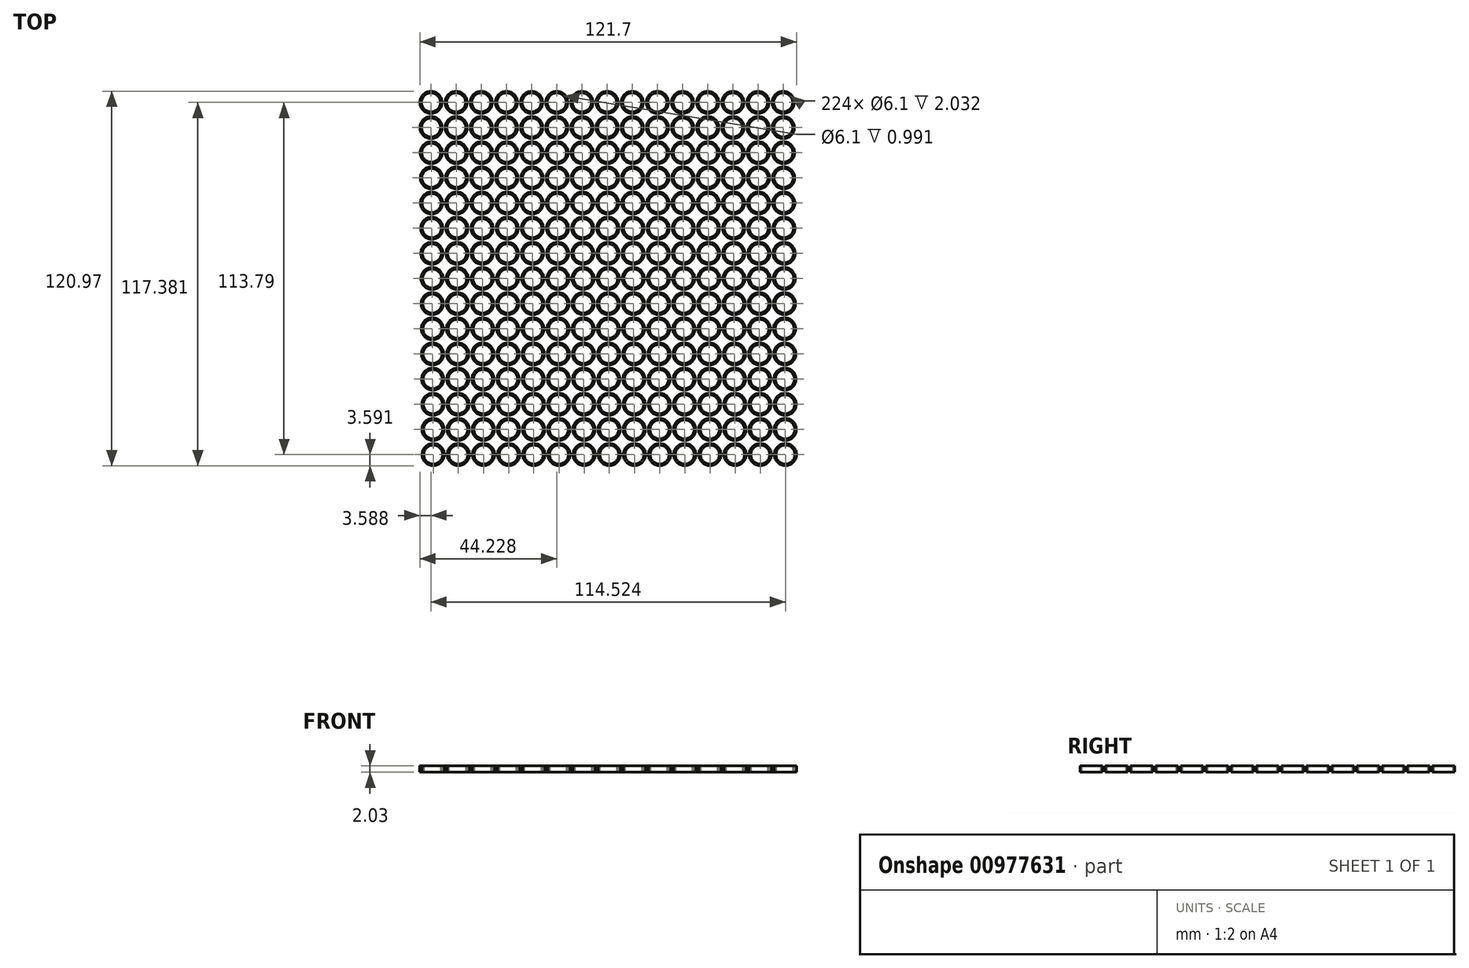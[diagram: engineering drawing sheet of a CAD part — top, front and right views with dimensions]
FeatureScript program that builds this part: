
annotation { "Feature Type Name" : "Feature", "Feature Type Description" : "" }
export const myFeature = defineFeature(function(context is Context, id is Id, definition is map)
    precondition{}
    {
        {
            var Q0;
            Q0=qCreatedBy(makeId("Top.planeOp"),FACE);
            var sketch = newSketch(context, id + "F0", { "sketchPlane" : qUnion([Q0])});
            skCircle(sketch, "E0", {"center": v(-60.84, 14.37) * mm, "radius": 3.6 * mm});
            skCircle(sketch, "E1.1.0.0", {"center": v(-52.71, 14.37) * mm, "radius": 3.6 * mm});
            skCircle(sketch, "E1.2.0.0", {"center": v(-44.59, 14.37) * mm, "radius": 3.6 * mm});
            skCircle(sketch, "E1.3.0.0", {"center": v(-36.46, 14.37) * mm, "radius": 3.6 * mm});
            skLineSegment(sketch, "E1.direction1", {"start": v(-60.84, 14.37) * mm, "end": v(-52.71, 14.37) * mm, "construction": true});
            skCircle(sketch, "E2.0.4.0", {"center": v(-28.33, 14.37) * mm, "radius": 3.6 * mm});
            skLineSegment(sketch, "E3.left", {"start": v(-60.84, 14.37) * mm, "end": v(-60.84, 14.37) * mm});
            skLineSegment(sketch, "E3.right", {"start": v(-28.33, 14.37) * mm, "end": v(-28.33, 14.37) * mm});
            skCircle(sketch, "E4", {"center": v(-60.84, 14.37) * mm, "radius": 3.05 * mm});
            skCircle(sketch, "E5.1.0.0", {"center": v(-52.71, 14.37) * mm, "radius": 3.05 * mm});
            skCircle(sketch, "E5.2.0.0", {"center": v(-44.59, 14.37) * mm, "radius": 3.05 * mm});
            skCircle(sketch, "E5.3.0.0", {"center": v(-36.46, 14.37) * mm, "radius": 3.05 * mm});
            skCircle(sketch, "E5.4.0.0", {"center": v(-28.33, 14.37) * mm, "radius": 3.05 * mm});
            skCircle(sketch, "E6", {"center": v(-60.84, 14.37) * mm, "radius": 2.54 * mm});
            skCircle(sketch, "E7.1.0.0", {"center": v(-52.71, 14.37) * mm, "radius": 2.54 * mm});
            skCircle(sketch, "E7.2.0.0", {"center": v(-44.59, 14.37) * mm, "radius": 2.54 * mm});
            skCircle(sketch, "E7.3.0.0", {"center": v(-36.46, 14.37) * mm, "radius": 2.54 * mm});
            skCircle(sketch, "E7.4.0.0", {"center": v(-28.33, 14.37) * mm, "radius": 2.54 * mm});
            skCircle(sketch, "E8.0.5.0", {"center": v(-20.2, 14.37) * mm, "radius": 2.54 * mm});
            skCircle(sketch, "E8.0.6.0", {"center": v(-12.07, 14.37) * mm, "radius": 2.54 * mm});
            skCircle(sketch, "E8.0.7.0", {"center": v(-3.95, 14.37) * mm, "radius": 2.54 * mm});
            skCircle(sketch, "E8.0.8.0", {"center": v(4.18, 14.37) * mm, "radius": 2.54 * mm});
            skCircle(sketch, "E8.0.9.0", {"center": v(12.31, 14.37) * mm, "radius": 2.54 * mm});
            skCircle(sketch, "E8.0.10.0", {"center": v(20.44, 14.37) * mm, "radius": 2.54 * mm});
            skCircle(sketch, "E8.0.11.0", {"center": v(28.57, 14.37) * mm, "radius": 2.54 * mm});
            skCircle(sketch, "E8.0.12.0", {"center": v(36.7, 14.37) * mm, "radius": 2.54 * mm});
            skCircle(sketch, "E8.0.13.0", {"center": v(44.82, 14.37) * mm, "radius": 2.54 * mm});
            skCircle(sketch, "E8.0.14.0", {"center": v(52.95, 14.37) * mm, "radius": 2.54 * mm});
            skCircle(sketch, "E9.0.5.0", {"center": v(-20.2, 14.37) * mm, "radius": 3.6 * mm});
            skCircle(sketch, "E9.0.6.0", {"center": v(-12.07, 14.37) * mm, "radius": 3.6 * mm});
            skCircle(sketch, "E9.0.7.0", {"center": v(-3.95, 14.37) * mm, "radius": 3.6 * mm});
            skCircle(sketch, "E9.0.8.0", {"center": v(4.18, 14.37) * mm, "radius": 3.6 * mm});
            skCircle(sketch, "E9.0.9.0", {"center": v(12.31, 14.37) * mm, "radius": 3.6 * mm});
            skCircle(sketch, "E9.0.10.0", {"center": v(20.44, 14.37) * mm, "radius": 3.6 * mm});
            skCircle(sketch, "E9.0.11.0", {"center": v(28.57, 14.37) * mm, "radius": 3.6 * mm});
            skCircle(sketch, "E9.0.12.0", {"center": v(36.7, 14.37) * mm, "radius": 3.6 * mm});
            skCircle(sketch, "E9.0.13.0", {"center": v(44.82, 14.37) * mm, "radius": 3.6 * mm});
            skCircle(sketch, "E9.0.14.0", {"center": v(52.95, 14.37) * mm, "radius": 3.6 * mm});
            skLineSegment(sketch, "E10.direction1", {"start": v(-60.84, 14.37) * mm, "end": v(-60.77, 6.24) * mm, "construction": true});
            skCircle(sketch, "E11.0.5.0", {"center": v(-20.2, 14.37) * mm, "radius": 3.05 * mm});
            skCircle(sketch, "E11.0.6.0", {"center": v(-12.07, 14.37) * mm, "radius": 3.05 * mm});
            skCircle(sketch, "E11.0.7.0", {"center": v(-3.95, 14.37) * mm, "radius": 3.05 * mm});
            skCircle(sketch, "E11.0.8.0", {"center": v(4.18, 14.37) * mm, "radius": 3.05 * mm});
            skCircle(sketch, "E11.0.9.0", {"center": v(12.31, 14.37) * mm, "radius": 3.05 * mm});
            skCircle(sketch, "E11.0.10.0", {"center": v(20.44, 14.37) * mm, "radius": 3.05 * mm});
            skCircle(sketch, "E11.0.11.0", {"center": v(28.57, 14.37) * mm, "radius": 3.05 * mm});
            skCircle(sketch, "E11.0.12.0", {"center": v(36.7, 14.37) * mm, "radius": 3.05 * mm});
            skCircle(sketch, "E11.0.13.0", {"center": v(44.82, 14.37) * mm, "radius": 3.05 * mm});
            skCircle(sketch, "E11.0.14.0", {"center": v(52.95, 14.37) * mm, "radius": 3.05 * mm});
            skCircle(sketch, "E12.1.0.0", {"center": v(44.87, 6.24) * mm, "radius": 2.54 * mm});
            skCircle(sketch, "E12.1.0.1", {"center": v(-52.66, 6.24) * mm, "radius": 2.54 * mm});
            skLineSegment(sketch, "E12.1.0.2", {"start": v(-60.79, 6.24) * mm, "end": v(-52.66, 6.24) * mm, "construction": true});
            skCircle(sketch, "E12.1.0.3", {"center": v(-36.4, 6.24) * mm, "radius": 3.6 * mm});
            skCircle(sketch, "E12.1.0.4", {"center": v(-3.9, 6.24) * mm, "radius": 3.6 * mm});
            skCircle(sketch, "E12.1.0.5", {"center": v(44.87, 6.24) * mm, "radius": 3.6 * mm});
            skCircle(sketch, "E12.1.0.6", {"center": v(36.75, 6.24) * mm, "radius": 3.6 * mm});
            skCircle(sketch, "E12.1.0.7", {"center": v(53, 6.24) * mm, "radius": 3.6 * mm});
            skCircle(sketch, "E12.1.0.8", {"center": v(-12.02, 6.24) * mm, "radius": 3.05 * mm});
            skCircle(sketch, "E12.1.0.9", {"center": v(20.5, 6.24) * mm, "radius": 3.6 * mm});
            skCircle(sketch, "E12.1.0.10", {"center": v(-12.02, 6.24) * mm, "radius": 2.54 * mm});
            skCircle(sketch, "E12.1.0.11", {"center": v(28.62, 6.24) * mm, "radius": 2.54 * mm});
            skCircle(sketch, "E12.1.0.12", {"center": v(4.23, 6.24) * mm, "radius": 2.54 * mm});
            skCircle(sketch, "E12.1.0.13", {"center": v(-28.28, 6.24) * mm, "radius": 3.6 * mm});
            skCircle(sketch, "E12.1.0.14", {"center": v(-28.28, 6.24) * mm, "radius": 3.05 * mm});
            skCircle(sketch, "E12.1.0.15", {"center": v(4.23, 6.24) * mm, "radius": 3.6 * mm});
            skCircle(sketch, "E12.1.0.16", {"center": v(12.36, 6.24) * mm, "radius": 3.6 * mm});
            skCircle(sketch, "E12.1.0.17", {"center": v(-20.15, 6.24) * mm, "radius": 2.54 * mm});
            skCircle(sketch, "E12.1.0.18", {"center": v(-20.15, 6.24) * mm, "radius": 3.05 * mm});
            skCircle(sketch, "E12.1.0.19", {"center": v(28.62, 6.24) * mm, "radius": 3.05 * mm});
            skLineSegment(sketch, "E12.1.0.20", {"start": v(-60.79, 6.24) * mm, "end": v(-60.72, -1.88) * mm, "construction": true});
            skCircle(sketch, "E12.1.0.21", {"center": v(-36.4, 6.24) * mm, "radius": 3.05 * mm});
            skCircle(sketch, "E12.1.0.22", {"center": v(-12.02, 6.24) * mm, "radius": 3.6 * mm});
            skCircle(sketch, "E12.1.0.23", {"center": v(-44.53, 6.24) * mm, "radius": 3.05 * mm});
            skCircle(sketch, "E12.1.0.24", {"center": v(28.62, 6.24) * mm, "radius": 3.6 * mm});
            skCircle(sketch, "E12.1.0.25", {"center": v(-20.15, 6.24) * mm, "radius": 3.6 * mm});
            skCircle(sketch, "E12.1.0.26", {"center": v(-44.53, 6.24) * mm, "radius": 2.54 * mm});
            skCircle(sketch, "E12.1.0.27", {"center": v(-60.79, 6.24) * mm, "radius": 3.6 * mm});
            skCircle(sketch, "E12.1.0.28", {"center": v(-36.4, 6.24) * mm, "radius": 2.54 * mm});
            skCircle(sketch, "E12.1.0.29", {"center": v(20.5, 6.24) * mm, "radius": 3.05 * mm});
            skCircle(sketch, "E12.1.0.30", {"center": v(-52.66, 6.24) * mm, "radius": 3.05 * mm});
            skCircle(sketch, "E12.1.0.31", {"center": v(53, 6.24) * mm, "radius": 3.05 * mm});
            skCircle(sketch, "E12.1.0.32", {"center": v(-3.9, 6.24) * mm, "radius": 3.05 * mm});
            skCircle(sketch, "E12.1.0.33", {"center": v(12.36, 6.24) * mm, "radius": 2.54 * mm});
            skCircle(sketch, "E12.1.0.34", {"center": v(36.75, 6.24) * mm, "radius": 2.54 * mm});
            skCircle(sketch, "E12.1.0.35", {"center": v(-44.53, 6.24) * mm, "radius": 3.6 * mm});
            skCircle(sketch, "E12.1.0.36", {"center": v(-52.66, 6.24) * mm, "radius": 3.6 * mm});
            skCircle(sketch, "E12.1.0.37", {"center": v(-3.9, 6.24) * mm, "radius": 2.54 * mm});
            skCircle(sketch, "E12.1.0.38", {"center": v(36.75, 6.24) * mm, "radius": 3.05 * mm});
            skCircle(sketch, "E12.1.0.39", {"center": v(4.23, 6.24) * mm, "radius": 3.05 * mm});
            skCircle(sketch, "E12.1.0.40", {"center": v(12.36, 6.24) * mm, "radius": 3.05 * mm});
            skCircle(sketch, "E12.1.0.41", {"center": v(53, 6.24) * mm, "radius": 2.54 * mm});
            skCircle(sketch, "E12.1.0.42", {"center": v(20.5, 6.24) * mm, "radius": 2.54 * mm});
            skCircle(sketch, "E12.1.0.43", {"center": v(-60.79, 6.24) * mm, "radius": 3.05 * mm});
            skCircle(sketch, "E12.1.0.44", {"center": v(44.87, 6.24) * mm, "radius": 3.05 * mm});
            skLineSegment(sketch, "E12.1.0.45", {"start": v(-60.79, 6.24) * mm, "end": v(-52.66, 6.24) * mm, "construction": true});
            skCircle(sketch, "E12.1.0.46", {"center": v(-60.79, 6.24) * mm, "radius": 2.54 * mm});
            skCircle(sketch, "E12.1.0.47", {"center": v(-28.28, 6.24) * mm, "radius": 2.54 * mm});
            skLineSegment(sketch, "E12.1.0.48", {"start": v(-60.79, 6.24) * mm, "end": v(-52.66, 6.24) * mm, "construction": true});
            skCircle(sketch, "E12.2.0.0", {"center": v(44.93, -1.88) * mm, "radius": 2.54 * mm});
            skCircle(sketch, "E12.2.0.1", {"center": v(-52.6, -1.88) * mm, "radius": 2.54 * mm});
            skLineSegment(sketch, "E12.2.0.2", {"start": v(-60.74, -1.88) * mm, "end": v(-52.6, -1.88) * mm, "construction": true});
            skCircle(sketch, "E12.2.0.3", {"center": v(-36.35, -1.88) * mm, "radius": 3.6 * mm});
            skCircle(sketch, "E12.2.0.4", {"center": v(-3.84, -1.88) * mm, "radius": 3.6 * mm});
            skCircle(sketch, "E12.2.0.5", {"center": v(44.93, -1.88) * mm, "radius": 3.6 * mm});
            skCircle(sketch, "E12.2.0.6", {"center": v(36.8, -1.88) * mm, "radius": 3.6 * mm});
            skCircle(sketch, "E12.2.0.7", {"center": v(53.05, -1.88) * mm, "radius": 3.6 * mm});
            skCircle(sketch, "E12.2.0.8", {"center": v(-11.97, -1.88) * mm, "radius": 3.05 * mm});
            skCircle(sketch, "E12.2.0.9", {"center": v(20.54, -1.88) * mm, "radius": 3.6 * mm});
            skCircle(sketch, "E12.2.0.10", {"center": v(-11.97, -1.88) * mm, "radius": 2.54 * mm});
            skCircle(sketch, "E12.2.0.11", {"center": v(28.67, -1.88) * mm, "radius": 2.54 * mm});
            skCircle(sketch, "E12.2.0.12", {"center": v(4.29, -1.88) * mm, "radius": 2.54 * mm});
            skCircle(sketch, "E12.2.0.13", {"center": v(-28.23, -1.88) * mm, "radius": 3.6 * mm});
            skCircle(sketch, "E12.2.0.14", {"center": v(-28.23, -1.88) * mm, "radius": 3.05 * mm});
            skCircle(sketch, "E12.2.0.15", {"center": v(4.29, -1.88) * mm, "radius": 3.6 * mm});
            skCircle(sketch, "E12.2.0.16", {"center": v(12.41, -1.88) * mm, "radius": 3.6 * mm});
            skCircle(sketch, "E12.2.0.17", {"center": v(-20.1, -1.88) * mm, "radius": 2.54 * mm});
            skCircle(sketch, "E12.2.0.18", {"center": v(-20.1, -1.88) * mm, "radius": 3.05 * mm});
            skCircle(sketch, "E12.2.0.19", {"center": v(28.67, -1.88) * mm, "radius": 3.05 * mm});
            skLineSegment(sketch, "E12.2.0.20", {"start": v(-60.74, -1.88) * mm, "end": v(-60.67, -10.01) * mm, "construction": true});
            skCircle(sketch, "E12.2.0.21", {"center": v(-36.35, -1.88) * mm, "radius": 3.05 * mm});
            skCircle(sketch, "E12.2.0.22", {"center": v(-11.97, -1.88) * mm, "radius": 3.6 * mm});
            skCircle(sketch, "E12.2.0.23", {"center": v(-44.48, -1.88) * mm, "radius": 3.05 * mm});
            skCircle(sketch, "E12.2.0.24", {"center": v(28.67, -1.88) * mm, "radius": 3.6 * mm});
            skCircle(sketch, "E12.2.0.25", {"center": v(-20.1, -1.88) * mm, "radius": 3.6 * mm});
            skCircle(sketch, "E12.2.0.26", {"center": v(-44.48, -1.88) * mm, "radius": 2.54 * mm});
            skCircle(sketch, "E12.2.0.27", {"center": v(-60.74, -1.88) * mm, "radius": 3.6 * mm});
            skCircle(sketch, "E12.2.0.28", {"center": v(-36.35, -1.88) * mm, "radius": 2.54 * mm});
            skCircle(sketch, "E12.2.0.29", {"center": v(20.54, -1.88) * mm, "radius": 3.05 * mm});
            skCircle(sketch, "E12.2.0.30", {"center": v(-52.6, -1.88) * mm, "radius": 3.05 * mm});
            skCircle(sketch, "E12.2.0.31", {"center": v(53.05, -1.88) * mm, "radius": 3.05 * mm});
            skCircle(sketch, "E12.2.0.32", {"center": v(-3.84, -1.88) * mm, "radius": 3.05 * mm});
            skCircle(sketch, "E12.2.0.33", {"center": v(12.41, -1.88) * mm, "radius": 2.54 * mm});
            skCircle(sketch, "E12.2.0.34", {"center": v(36.8, -1.88) * mm, "radius": 2.54 * mm});
            skCircle(sketch, "E12.2.0.35", {"center": v(-44.48, -1.88) * mm, "radius": 3.6 * mm});
            skCircle(sketch, "E12.2.0.36", {"center": v(-52.6, -1.88) * mm, "radius": 3.6 * mm});
            skCircle(sketch, "E12.2.0.37", {"center": v(-3.84, -1.88) * mm, "radius": 2.54 * mm});
            skCircle(sketch, "E12.2.0.38", {"center": v(36.8, -1.88) * mm, "radius": 3.05 * mm});
            skCircle(sketch, "E12.2.0.39", {"center": v(4.29, -1.88) * mm, "radius": 3.05 * mm});
            skCircle(sketch, "E12.2.0.40", {"center": v(12.41, -1.88) * mm, "radius": 3.05 * mm});
            skCircle(sketch, "E12.2.0.41", {"center": v(53.05, -1.88) * mm, "radius": 2.54 * mm});
            skCircle(sketch, "E12.2.0.42", {"center": v(20.54, -1.88) * mm, "radius": 2.54 * mm});
            skCircle(sketch, "E12.2.0.43", {"center": v(-60.74, -1.88) * mm, "radius": 3.05 * mm});
            skCircle(sketch, "E12.2.0.44", {"center": v(44.93, -1.88) * mm, "radius": 3.05 * mm});
            skLineSegment(sketch, "E12.2.0.45", {"start": v(-60.74, -1.88) * mm, "end": v(-52.6, -1.88) * mm, "construction": true});
            skCircle(sketch, "E12.2.0.46", {"center": v(-60.74, -1.88) * mm, "radius": 2.54 * mm});
            skCircle(sketch, "E12.2.0.47", {"center": v(-28.23, -1.88) * mm, "radius": 2.54 * mm});
            skLineSegment(sketch, "E12.2.0.48", {"start": v(-60.74, -1.88) * mm, "end": v(-52.6, -1.88) * mm, "construction": true});
            skCircle(sketch, "E12.3.0.0", {"center": v(44.98, -10.01) * mm, "radius": 2.54 * mm});
            skCircle(sketch, "E12.3.0.1", {"center": v(-52.56, -10.01) * mm, "radius": 2.54 * mm});
            skLineSegment(sketch, "E12.3.0.2", {"start": v(-60.68, -10.01) * mm, "end": v(-52.56, -10.01) * mm, "construction": true});
            skCircle(sketch, "E12.3.0.3", {"center": v(-36.3, -10.01) * mm, "radius": 3.6 * mm});
            skCircle(sketch, "E12.3.0.4", {"center": v(-3.79, -10.01) * mm, "radius": 3.6 * mm});
            skCircle(sketch, "E12.3.0.5", {"center": v(44.98, -10.01) * mm, "radius": 3.6 * mm});
            skCircle(sketch, "E12.3.0.6", {"center": v(36.85, -10.01) * mm, "radius": 3.6 * mm});
            skCircle(sketch, "E12.3.0.7", {"center": v(53.1, -10.01) * mm, "radius": 3.6 * mm});
            skCircle(sketch, "E12.3.0.8", {"center": v(-11.92, -10.01) * mm, "radius": 3.05 * mm});
            skCircle(sketch, "E12.3.0.9", {"center": v(20.6, -10.01) * mm, "radius": 3.6 * mm});
            skCircle(sketch, "E12.3.0.10", {"center": v(-11.92, -10.01) * mm, "radius": 2.54 * mm});
            skCircle(sketch, "E12.3.0.11", {"center": v(28.72, -10.01) * mm, "radius": 2.54 * mm});
            skCircle(sketch, "E12.3.0.12", {"center": v(4.34, -10.01) * mm, "radius": 2.54 * mm});
            skCircle(sketch, "E12.3.0.13", {"center": v(-28.17, -10.01) * mm, "radius": 3.6 * mm});
            skCircle(sketch, "E12.3.0.14", {"center": v(-28.17, -10.01) * mm, "radius": 3.05 * mm});
            skCircle(sketch, "E12.3.0.15", {"center": v(4.34, -10.01) * mm, "radius": 3.6 * mm});
            skCircle(sketch, "E12.3.0.16", {"center": v(12.47, -10.01) * mm, "radius": 3.6 * mm});
            skCircle(sketch, "E12.3.0.17", {"center": v(-20.04, -10.01) * mm, "radius": 2.54 * mm});
            skCircle(sketch, "E12.3.0.18", {"center": v(-20.04, -10.01) * mm, "radius": 3.05 * mm});
            skCircle(sketch, "E12.3.0.19", {"center": v(28.72, -10.01) * mm, "radius": 3.05 * mm});
            skLineSegment(sketch, "E12.3.0.20", {"start": v(-60.68, -10.01) * mm, "end": v(-60.62, -18.14) * mm, "construction": true});
            skCircle(sketch, "E12.3.0.21", {"center": v(-36.3, -10.01) * mm, "radius": 3.05 * mm});
            skCircle(sketch, "E12.3.0.22", {"center": v(-11.92, -10.01) * mm, "radius": 3.6 * mm});
            skCircle(sketch, "E12.3.0.23", {"center": v(-44.43, -10.01) * mm, "radius": 3.05 * mm});
            skCircle(sketch, "E12.3.0.24", {"center": v(28.72, -10.01) * mm, "radius": 3.6 * mm});
            skCircle(sketch, "E12.3.0.25", {"center": v(-20.04, -10.01) * mm, "radius": 3.6 * mm});
            skCircle(sketch, "E12.3.0.26", {"center": v(-44.43, -10.01) * mm, "radius": 2.54 * mm});
            skCircle(sketch, "E12.3.0.27", {"center": v(-60.68, -10.01) * mm, "radius": 3.6 * mm});
            skCircle(sketch, "E12.3.0.28", {"center": v(-36.3, -10.01) * mm, "radius": 2.54 * mm});
            skCircle(sketch, "E12.3.0.29", {"center": v(20.6, -10.01) * mm, "radius": 3.05 * mm});
            skCircle(sketch, "E12.3.0.30", {"center": v(-52.56, -10.01) * mm, "radius": 3.05 * mm});
            skCircle(sketch, "E12.3.0.31", {"center": v(53.1, -10.01) * mm, "radius": 3.05 * mm});
            skCircle(sketch, "E12.3.0.32", {"center": v(-3.79, -10.01) * mm, "radius": 3.05 * mm});
            skCircle(sketch, "E12.3.0.33", {"center": v(12.47, -10.01) * mm, "radius": 2.54 * mm});
            skCircle(sketch, "E12.3.0.34", {"center": v(36.85, -10.01) * mm, "radius": 2.54 * mm});
            skCircle(sketch, "E12.3.0.35", {"center": v(-44.43, -10.01) * mm, "radius": 3.6 * mm});
            skCircle(sketch, "E12.3.0.36", {"center": v(-52.56, -10.01) * mm, "radius": 3.6 * mm});
            skCircle(sketch, "E12.3.0.37", {"center": v(-3.79, -10.01) * mm, "radius": 2.54 * mm});
            skCircle(sketch, "E12.3.0.38", {"center": v(36.85, -10.01) * mm, "radius": 3.05 * mm});
            skCircle(sketch, "E12.3.0.39", {"center": v(4.34, -10.01) * mm, "radius": 3.05 * mm});
            skCircle(sketch, "E12.3.0.40", {"center": v(12.47, -10.01) * mm, "radius": 3.05 * mm});
            skCircle(sketch, "E12.3.0.41", {"center": v(53.1, -10.01) * mm, "radius": 2.54 * mm});
            skCircle(sketch, "E12.3.0.42", {"center": v(20.6, -10.01) * mm, "radius": 2.54 * mm});
            skCircle(sketch, "E12.3.0.43", {"center": v(-60.68, -10.01) * mm, "radius": 3.05 * mm});
            skCircle(sketch, "E12.3.0.44", {"center": v(44.98, -10.01) * mm, "radius": 3.05 * mm});
            skLineSegment(sketch, "E12.3.0.45", {"start": v(-60.68, -10.01) * mm, "end": v(-52.56, -10.01) * mm, "construction": true});
            skCircle(sketch, "E12.3.0.46", {"center": v(-60.68, -10.01) * mm, "radius": 2.54 * mm});
            skCircle(sketch, "E12.3.0.47", {"center": v(-28.17, -10.01) * mm, "radius": 2.54 * mm});
            skLineSegment(sketch, "E12.3.0.48", {"start": v(-60.68, -10.01) * mm, "end": v(-52.56, -10.01) * mm, "construction": true});
            skCircle(sketch, "E12.4.0.0", {"center": v(45.03, -18.14) * mm, "radius": 2.54 * mm});
            skCircle(sketch, "E12.4.0.1", {"center": v(-52.5, -18.14) * mm, "radius": 2.54 * mm});
            skLineSegment(sketch, "E12.4.0.2", {"start": v(-60.63, -18.14) * mm, "end": v(-52.5, -18.14) * mm, "construction": true});
            skCircle(sketch, "E12.4.0.3", {"center": v(-36.25, -18.14) * mm, "radius": 3.6 * mm});
            skCircle(sketch, "E12.4.0.4", {"center": v(-3.74, -18.14) * mm, "radius": 3.6 * mm});
            skCircle(sketch, "E12.4.0.5", {"center": v(45.03, -18.14) * mm, "radius": 3.6 * mm});
            skCircle(sketch, "E12.4.0.6", {"center": v(36.9, -18.14) * mm, "radius": 3.6 * mm});
            skCircle(sketch, "E12.4.0.7", {"center": v(53.16, -18.14) * mm, "radius": 3.6 * mm});
            skCircle(sketch, "E12.4.0.8", {"center": v(-11.86, -18.14) * mm, "radius": 3.05 * mm});
            skCircle(sketch, "E12.4.0.9", {"center": v(20.65, -18.14) * mm, "radius": 3.6 * mm});
            skCircle(sketch, "E12.4.0.10", {"center": v(-11.86, -18.14) * mm, "radius": 2.54 * mm});
            skCircle(sketch, "E12.4.0.11", {"center": v(28.78, -18.14) * mm, "radius": 2.54 * mm});
            skCircle(sketch, "E12.4.0.12", {"center": v(4.4, -18.14) * mm, "radius": 2.54 * mm});
            skCircle(sketch, "E12.4.0.13", {"center": v(-28.12, -18.14) * mm, "radius": 3.6 * mm});
            skCircle(sketch, "E12.4.0.14", {"center": v(-28.12, -18.14) * mm, "radius": 3.05 * mm});
            skCircle(sketch, "E12.4.0.15", {"center": v(4.4, -18.14) * mm, "radius": 3.6 * mm});
            skCircle(sketch, "E12.4.0.16", {"center": v(12.52, -18.14) * mm, "radius": 3.6 * mm});
            skCircle(sketch, "E12.4.0.17", {"center": v(-20, -18.14) * mm, "radius": 2.54 * mm});
            skCircle(sketch, "E12.4.0.18", {"center": v(-20, -18.14) * mm, "radius": 3.05 * mm});
            skCircle(sketch, "E12.4.0.19", {"center": v(28.78, -18.14) * mm, "radius": 3.05 * mm});
            skLineSegment(sketch, "E12.4.0.20", {"start": v(-60.63, -18.14) * mm, "end": v(-60.56, -26.27) * mm, "construction": true});
            skCircle(sketch, "E12.4.0.21", {"center": v(-36.25, -18.14) * mm, "radius": 3.05 * mm});
            skCircle(sketch, "E12.4.0.22", {"center": v(-11.86, -18.14) * mm, "radius": 3.6 * mm});
            skCircle(sketch, "E12.4.0.23", {"center": v(-44.38, -18.14) * mm, "radius": 3.05 * mm});
            skCircle(sketch, "E12.4.0.24", {"center": v(28.78, -18.14) * mm, "radius": 3.6 * mm});
            skCircle(sketch, "E12.4.0.25", {"center": v(-20, -18.14) * mm, "radius": 3.6 * mm});
            skCircle(sketch, "E12.4.0.26", {"center": v(-44.38, -18.14) * mm, "radius": 2.54 * mm});
            skCircle(sketch, "E12.4.0.27", {"center": v(-60.63, -18.14) * mm, "radius": 3.6 * mm});
            skCircle(sketch, "E12.4.0.28", {"center": v(-36.25, -18.14) * mm, "radius": 2.54 * mm});
            skCircle(sketch, "E12.4.0.29", {"center": v(20.65, -18.14) * mm, "radius": 3.05 * mm});
            skCircle(sketch, "E12.4.0.30", {"center": v(-52.5, -18.14) * mm, "radius": 3.05 * mm});
            skCircle(sketch, "E12.4.0.31", {"center": v(53.16, -18.14) * mm, "radius": 3.05 * mm});
            skCircle(sketch, "E12.4.0.32", {"center": v(-3.74, -18.14) * mm, "radius": 3.05 * mm});
            skCircle(sketch, "E12.4.0.33", {"center": v(12.52, -18.14) * mm, "radius": 2.54 * mm});
            skCircle(sketch, "E12.4.0.34", {"center": v(36.9, -18.14) * mm, "radius": 2.54 * mm});
            skCircle(sketch, "E12.4.0.35", {"center": v(-44.38, -18.14) * mm, "radius": 3.6 * mm});
            skCircle(sketch, "E12.4.0.36", {"center": v(-52.5, -18.14) * mm, "radius": 3.6 * mm});
            skCircle(sketch, "E12.4.0.37", {"center": v(-3.74, -18.14) * mm, "radius": 2.54 * mm});
            skCircle(sketch, "E12.4.0.38", {"center": v(36.9, -18.14) * mm, "radius": 3.05 * mm});
            skCircle(sketch, "E12.4.0.39", {"center": v(4.4, -18.14) * mm, "radius": 3.05 * mm});
            skCircle(sketch, "E12.4.0.40", {"center": v(12.52, -18.14) * mm, "radius": 3.05 * mm});
            skCircle(sketch, "E12.4.0.41", {"center": v(53.16, -18.14) * mm, "radius": 2.54 * mm});
            skCircle(sketch, "E12.4.0.42", {"center": v(20.65, -18.14) * mm, "radius": 2.54 * mm});
            skCircle(sketch, "E12.4.0.43", {"center": v(-60.63, -18.14) * mm, "radius": 3.05 * mm});
            skCircle(sketch, "E12.4.0.44", {"center": v(45.03, -18.14) * mm, "radius": 3.05 * mm});
            skLineSegment(sketch, "E12.4.0.45", {"start": v(-60.63, -18.14) * mm, "end": v(-52.5, -18.14) * mm, "construction": true});
            skCircle(sketch, "E12.4.0.46", {"center": v(-60.63, -18.14) * mm, "radius": 2.54 * mm});
            skCircle(sketch, "E12.4.0.47", {"center": v(-28.12, -18.14) * mm, "radius": 2.54 * mm});
            skLineSegment(sketch, "E12.4.0.48", {"start": v(-60.63, -18.14) * mm, "end": v(-52.5, -18.14) * mm, "construction": true});
            skCircle(sketch, "E12.5.0.0", {"center": v(45.08, -26.27) * mm, "radius": 2.54 * mm});
            skCircle(sketch, "E12.5.0.1", {"center": v(-52.45, -26.27) * mm, "radius": 2.54 * mm});
            skLineSegment(sketch, "E12.5.0.2", {"start": v(-60.58, -26.27) * mm, "end": v(-52.45, -26.27) * mm, "construction": true});
            skCircle(sketch, "E12.5.0.3", {"center": v(-36.2, -26.27) * mm, "radius": 3.6 * mm});
            skCircle(sketch, "E12.5.0.4", {"center": v(-3.68, -26.27) * mm, "radius": 3.6 * mm});
            skCircle(sketch, "E12.5.0.5", {"center": v(45.08, -26.27) * mm, "radius": 3.6 * mm});
            skCircle(sketch, "E12.5.0.6", {"center": v(36.96, -26.27) * mm, "radius": 3.6 * mm});
            skCircle(sketch, "E12.5.0.7", {"center": v(53.21, -26.27) * mm, "radius": 3.6 * mm});
            skCircle(sketch, "E12.5.0.8", {"center": v(-11.81, -26.27) * mm, "radius": 3.05 * mm});
            skCircle(sketch, "E12.5.0.9", {"center": v(20.7, -26.27) * mm, "radius": 3.6 * mm});
            skCircle(sketch, "E12.5.0.10", {"center": v(-11.81, -26.27) * mm, "radius": 2.54 * mm});
            skCircle(sketch, "E12.5.0.11", {"center": v(28.83, -26.27) * mm, "radius": 2.54 * mm});
            skCircle(sketch, "E12.5.0.12", {"center": v(4.44, -26.27) * mm, "radius": 2.54 * mm});
            skCircle(sketch, "E12.5.0.13", {"center": v(-28.07, -26.27) * mm, "radius": 3.6 * mm});
            skCircle(sketch, "E12.5.0.14", {"center": v(-28.07, -26.27) * mm, "radius": 3.05 * mm});
            skCircle(sketch, "E12.5.0.15", {"center": v(4.44, -26.27) * mm, "radius": 3.6 * mm});
            skCircle(sketch, "E12.5.0.16", {"center": v(12.57, -26.27) * mm, "radius": 3.6 * mm});
            skCircle(sketch, "E12.5.0.17", {"center": v(-19.94, -26.27) * mm, "radius": 2.54 * mm});
            skCircle(sketch, "E12.5.0.18", {"center": v(-19.94, -26.27) * mm, "radius": 3.05 * mm});
            skCircle(sketch, "E12.5.0.19", {"center": v(28.83, -26.27) * mm, "radius": 3.05 * mm});
            skLineSegment(sketch, "E12.5.0.20", {"start": v(-60.58, -26.27) * mm, "end": v(-60.51, -34.4) * mm, "construction": true});
            skCircle(sketch, "E12.5.0.21", {"center": v(-36.2, -26.27) * mm, "radius": 3.05 * mm});
            skCircle(sketch, "E12.5.0.22", {"center": v(-11.81, -26.27) * mm, "radius": 3.6 * mm});
            skCircle(sketch, "E12.5.0.23", {"center": v(-44.32, -26.27) * mm, "radius": 3.05 * mm});
            skCircle(sketch, "E12.5.0.24", {"center": v(28.83, -26.27) * mm, "radius": 3.6 * mm});
            skCircle(sketch, "E12.5.0.25", {"center": v(-19.94, -26.27) * mm, "radius": 3.6 * mm});
            skCircle(sketch, "E12.5.0.26", {"center": v(-44.32, -26.27) * mm, "radius": 2.54 * mm});
            skCircle(sketch, "E12.5.0.27", {"center": v(-60.58, -26.27) * mm, "radius": 3.6 * mm});
            skCircle(sketch, "E12.5.0.28", {"center": v(-36.2, -26.27) * mm, "radius": 2.54 * mm});
            skCircle(sketch, "E12.5.0.29", {"center": v(20.7, -26.27) * mm, "radius": 3.05 * mm});
            skCircle(sketch, "E12.5.0.30", {"center": v(-52.45, -26.27) * mm, "radius": 3.05 * mm});
            skCircle(sketch, "E12.5.0.31", {"center": v(53.21, -26.27) * mm, "radius": 3.05 * mm});
            skCircle(sketch, "E12.5.0.32", {"center": v(-3.68, -26.27) * mm, "radius": 3.05 * mm});
            skCircle(sketch, "E12.5.0.33", {"center": v(12.57, -26.27) * mm, "radius": 2.54 * mm});
            skCircle(sketch, "E12.5.0.34", {"center": v(36.96, -26.27) * mm, "radius": 2.54 * mm});
            skCircle(sketch, "E12.5.0.35", {"center": v(-44.32, -26.27) * mm, "radius": 3.6 * mm});
            skCircle(sketch, "E12.5.0.36", {"center": v(-52.45, -26.27) * mm, "radius": 3.6 * mm});
            skCircle(sketch, "E12.5.0.37", {"center": v(-3.68, -26.27) * mm, "radius": 2.54 * mm});
            skCircle(sketch, "E12.5.0.38", {"center": v(36.96, -26.27) * mm, "radius": 3.05 * mm});
            skCircle(sketch, "E12.5.0.39", {"center": v(4.44, -26.27) * mm, "radius": 3.05 * mm});
            skCircle(sketch, "E12.5.0.40", {"center": v(12.57, -26.27) * mm, "radius": 3.05 * mm});
            skCircle(sketch, "E12.5.0.41", {"center": v(53.21, -26.27) * mm, "radius": 2.54 * mm});
            skCircle(sketch, "E12.5.0.42", {"center": v(20.7, -26.27) * mm, "radius": 2.54 * mm});
            skCircle(sketch, "E12.5.0.43", {"center": v(-60.58, -26.27) * mm, "radius": 3.05 * mm});
            skCircle(sketch, "E12.5.0.44", {"center": v(45.08, -26.27) * mm, "radius": 3.05 * mm});
            skLineSegment(sketch, "E12.5.0.45", {"start": v(-60.58, -26.27) * mm, "end": v(-52.45, -26.27) * mm, "construction": true});
            skCircle(sketch, "E12.5.0.46", {"center": v(-60.58, -26.27) * mm, "radius": 2.54 * mm});
            skCircle(sketch, "E12.5.0.47", {"center": v(-28.07, -26.27) * mm, "radius": 2.54 * mm});
            skLineSegment(sketch, "E12.5.0.48", {"start": v(-60.58, -26.27) * mm, "end": v(-52.45, -26.27) * mm, "construction": true});
            skCircle(sketch, "E12.6.0.0", {"center": v(45.14, -34.4) * mm, "radius": 2.54 * mm});
            skCircle(sketch, "E12.6.0.1", {"center": v(-52.4, -34.4) * mm, "radius": 2.54 * mm});
            skLineSegment(sketch, "E12.6.0.2", {"start": v(-60.53, -34.4) * mm, "end": v(-52.4, -34.4) * mm, "construction": true});
            skCircle(sketch, "E12.6.0.3", {"center": v(-36.14, -34.4) * mm, "radius": 3.6 * mm});
            skCircle(sketch, "E12.6.0.4", {"center": v(-3.63, -34.4) * mm, "radius": 3.6 * mm});
            skCircle(sketch, "E12.6.0.5", {"center": v(45.14, -34.4) * mm, "radius": 3.6 * mm});
            skCircle(sketch, "E12.6.0.6", {"center": v(37, -34.4) * mm, "radius": 3.6 * mm});
            skCircle(sketch, "E12.6.0.7", {"center": v(53.26, -34.4) * mm, "radius": 3.6 * mm});
            skCircle(sketch, "E12.6.0.8", {"center": v(-11.76, -34.4) * mm, "radius": 3.05 * mm});
            skCircle(sketch, "E12.6.0.9", {"center": v(20.75, -34.4) * mm, "radius": 3.6 * mm});
            skCircle(sketch, "E12.6.0.10", {"center": v(-11.76, -34.4) * mm, "radius": 2.54 * mm});
            skCircle(sketch, "E12.6.0.11", {"center": v(28.88, -34.4) * mm, "radius": 2.54 * mm});
            skCircle(sketch, "E12.6.0.12", {"center": v(4.5, -34.4) * mm, "radius": 2.54 * mm});
            skCircle(sketch, "E12.6.0.13", {"center": v(-28.02, -34.4) * mm, "radius": 3.6 * mm});
            skCircle(sketch, "E12.6.0.14", {"center": v(-28.02, -34.4) * mm, "radius": 3.05 * mm});
            skCircle(sketch, "E12.6.0.15", {"center": v(4.5, -34.4) * mm, "radius": 3.6 * mm});
            skCircle(sketch, "E12.6.0.16", {"center": v(12.62, -34.4) * mm, "radius": 3.6 * mm});
            skCircle(sketch, "E12.6.0.17", {"center": v(-19.89, -34.4) * mm, "radius": 2.54 * mm});
            skCircle(sketch, "E12.6.0.18", {"center": v(-19.89, -34.4) * mm, "radius": 3.05 * mm});
            skCircle(sketch, "E12.6.0.19", {"center": v(28.88, -34.4) * mm, "radius": 3.05 * mm});
            skLineSegment(sketch, "E12.6.0.20", {"start": v(-60.53, -34.4) * mm, "end": v(-60.46, -42.52) * mm, "construction": true});
            skCircle(sketch, "E12.6.0.21", {"center": v(-36.14, -34.4) * mm, "radius": 3.05 * mm});
            skCircle(sketch, "E12.6.0.22", {"center": v(-11.76, -34.4) * mm, "radius": 3.6 * mm});
            skCircle(sketch, "E12.6.0.23", {"center": v(-44.27, -34.4) * mm, "radius": 3.05 * mm});
            skCircle(sketch, "E12.6.0.24", {"center": v(28.88, -34.4) * mm, "radius": 3.6 * mm});
            skCircle(sketch, "E12.6.0.25", {"center": v(-19.89, -34.4) * mm, "radius": 3.6 * mm});
            skCircle(sketch, "E12.6.0.26", {"center": v(-44.27, -34.4) * mm, "radius": 2.54 * mm});
            skCircle(sketch, "E12.6.0.27", {"center": v(-60.53, -34.4) * mm, "radius": 3.6 * mm});
            skCircle(sketch, "E12.6.0.28", {"center": v(-36.14, -34.4) * mm, "radius": 2.54 * mm});
            skCircle(sketch, "E12.6.0.29", {"center": v(20.75, -34.4) * mm, "radius": 3.05 * mm});
            skCircle(sketch, "E12.6.0.30", {"center": v(-52.4, -34.4) * mm, "radius": 3.05 * mm});
            skCircle(sketch, "E12.6.0.31", {"center": v(53.26, -34.4) * mm, "radius": 3.05 * mm});
            skCircle(sketch, "E12.6.0.32", {"center": v(-3.63, -34.4) * mm, "radius": 3.05 * mm});
            skCircle(sketch, "E12.6.0.33", {"center": v(12.62, -34.4) * mm, "radius": 2.54 * mm});
            skCircle(sketch, "E12.6.0.34", {"center": v(37, -34.4) * mm, "radius": 2.54 * mm});
            skCircle(sketch, "E12.6.0.35", {"center": v(-44.27, -34.4) * mm, "radius": 3.6 * mm});
            skCircle(sketch, "E12.6.0.36", {"center": v(-52.4, -34.4) * mm, "radius": 3.6 * mm});
            skCircle(sketch, "E12.6.0.37", {"center": v(-3.63, -34.4) * mm, "radius": 2.54 * mm});
            skCircle(sketch, "E12.6.0.38", {"center": v(37, -34.4) * mm, "radius": 3.05 * mm});
            skCircle(sketch, "E12.6.0.39", {"center": v(4.5, -34.4) * mm, "radius": 3.05 * mm});
            skCircle(sketch, "E12.6.0.40", {"center": v(12.62, -34.4) * mm, "radius": 3.05 * mm});
            skCircle(sketch, "E12.6.0.41", {"center": v(53.26, -34.4) * mm, "radius": 2.54 * mm});
            skCircle(sketch, "E12.6.0.42", {"center": v(20.75, -34.4) * mm, "radius": 2.54 * mm});
            skCircle(sketch, "E12.6.0.43", {"center": v(-60.53, -34.4) * mm, "radius": 3.05 * mm});
            skCircle(sketch, "E12.6.0.44", {"center": v(45.14, -34.4) * mm, "radius": 3.05 * mm});
            skLineSegment(sketch, "E12.6.0.45", {"start": v(-60.53, -34.4) * mm, "end": v(-52.4, -34.4) * mm, "construction": true});
            skCircle(sketch, "E12.6.0.46", {"center": v(-60.53, -34.4) * mm, "radius": 2.54 * mm});
            skCircle(sketch, "E12.6.0.47", {"center": v(-28.02, -34.4) * mm, "radius": 2.54 * mm});
            skLineSegment(sketch, "E12.6.0.48", {"start": v(-60.53, -34.4) * mm, "end": v(-52.4, -34.4) * mm, "construction": true});
            skCircle(sketch, "E12.7.0.0", {"center": v(45.19, -42.52) * mm, "radius": 2.54 * mm});
            skCircle(sketch, "E12.7.0.1", {"center": v(-52.35, -42.52) * mm, "radius": 2.54 * mm});
            skLineSegment(sketch, "E12.7.0.2", {"start": v(-60.48, -42.52) * mm, "end": v(-52.35, -42.52) * mm, "construction": true});
            skCircle(sketch, "E12.7.0.3", {"center": v(-36.1, -42.52) * mm, "radius": 3.6 * mm});
            skCircle(sketch, "E12.7.0.4", {"center": v(-3.58, -42.52) * mm, "radius": 3.6 * mm});
            skCircle(sketch, "E12.7.0.5", {"center": v(45.19, -42.52) * mm, "radius": 3.6 * mm});
            skCircle(sketch, "E12.7.0.6", {"center": v(37.06, -42.52) * mm, "radius": 3.6 * mm});
            skCircle(sketch, "E12.7.0.7", {"center": v(53.32, -42.52) * mm, "radius": 3.6 * mm});
            skCircle(sketch, "E12.7.0.8", {"center": v(-11.7, -42.52) * mm, "radius": 3.05 * mm});
            skCircle(sketch, "E12.7.0.9", {"center": v(20.8, -42.52) * mm, "radius": 3.6 * mm});
            skCircle(sketch, "E12.7.0.10", {"center": v(-11.7, -42.52) * mm, "radius": 2.54 * mm});
            skCircle(sketch, "E12.7.0.11", {"center": v(28.93, -42.52) * mm, "radius": 2.54 * mm});
            skCircle(sketch, "E12.7.0.12", {"center": v(4.55, -42.52) * mm, "radius": 2.54 * mm});
            skCircle(sketch, "E12.7.0.13", {"center": v(-27.96, -42.52) * mm, "radius": 3.6 * mm});
            skCircle(sketch, "E12.7.0.14", {"center": v(-27.96, -42.52) * mm, "radius": 3.05 * mm});
            skCircle(sketch, "E12.7.0.15", {"center": v(4.55, -42.52) * mm, "radius": 3.6 * mm});
            skCircle(sketch, "E12.7.0.16", {"center": v(12.68, -42.52) * mm, "radius": 3.6 * mm});
            skCircle(sketch, "E12.7.0.17", {"center": v(-19.84, -42.52) * mm, "radius": 2.54 * mm});
            skCircle(sketch, "E12.7.0.18", {"center": v(-19.84, -42.52) * mm, "radius": 3.05 * mm});
            skCircle(sketch, "E12.7.0.19", {"center": v(28.93, -42.52) * mm, "radius": 3.05 * mm});
            skLineSegment(sketch, "E12.7.0.20", {"start": v(-60.48, -42.52) * mm, "end": v(-60.4, -50.65) * mm, "construction": true});
            skCircle(sketch, "E12.7.0.21", {"center": v(-36.1, -42.52) * mm, "radius": 3.05 * mm});
            skCircle(sketch, "E12.7.0.22", {"center": v(-11.7, -42.52) * mm, "radius": 3.6 * mm});
            skCircle(sketch, "E12.7.0.23", {"center": v(-44.22, -42.52) * mm, "radius": 3.05 * mm});
            skCircle(sketch, "E12.7.0.24", {"center": v(28.93, -42.52) * mm, "radius": 3.6 * mm});
            skCircle(sketch, "E12.7.0.25", {"center": v(-19.84, -42.52) * mm, "radius": 3.6 * mm});
            skCircle(sketch, "E12.7.0.26", {"center": v(-44.22, -42.52) * mm, "radius": 2.54 * mm});
            skCircle(sketch, "E12.7.0.27", {"center": v(-60.48, -42.52) * mm, "radius": 3.6 * mm});
            skCircle(sketch, "E12.7.0.28", {"center": v(-36.1, -42.52) * mm, "radius": 2.54 * mm});
            skCircle(sketch, "E12.7.0.29", {"center": v(20.8, -42.52) * mm, "radius": 3.05 * mm});
            skCircle(sketch, "E12.7.0.30", {"center": v(-52.35, -42.52) * mm, "radius": 3.05 * mm});
            skCircle(sketch, "E12.7.0.31", {"center": v(53.32, -42.52) * mm, "radius": 3.05 * mm});
            skCircle(sketch, "E12.7.0.32", {"center": v(-3.58, -42.52) * mm, "radius": 3.05 * mm});
            skCircle(sketch, "E12.7.0.33", {"center": v(12.68, -42.52) * mm, "radius": 2.54 * mm});
            skCircle(sketch, "E12.7.0.34", {"center": v(37.06, -42.52) * mm, "radius": 2.54 * mm});
            skCircle(sketch, "E12.7.0.35", {"center": v(-44.22, -42.52) * mm, "radius": 3.6 * mm});
            skCircle(sketch, "E12.7.0.36", {"center": v(-52.35, -42.52) * mm, "radius": 3.6 * mm});
            skCircle(sketch, "E12.7.0.37", {"center": v(-3.58, -42.52) * mm, "radius": 2.54 * mm});
            skCircle(sketch, "E12.7.0.38", {"center": v(37.06, -42.52) * mm, "radius": 3.05 * mm});
            skCircle(sketch, "E12.7.0.39", {"center": v(4.55, -42.52) * mm, "radius": 3.05 * mm});
            skCircle(sketch, "E12.7.0.40", {"center": v(12.68, -42.52) * mm, "radius": 3.05 * mm});
            skCircle(sketch, "E12.7.0.41", {"center": v(53.32, -42.52) * mm, "radius": 2.54 * mm});
            skCircle(sketch, "E12.7.0.42", {"center": v(20.8, -42.52) * mm, "radius": 2.54 * mm});
            skCircle(sketch, "E12.7.0.43", {"center": v(-60.48, -42.52) * mm, "radius": 3.05 * mm});
            skCircle(sketch, "E12.7.0.44", {"center": v(45.19, -42.52) * mm, "radius": 3.05 * mm});
            skLineSegment(sketch, "E12.7.0.45", {"start": v(-60.48, -42.52) * mm, "end": v(-52.35, -42.52) * mm, "construction": true});
            skCircle(sketch, "E12.7.0.46", {"center": v(-60.48, -42.52) * mm, "radius": 2.54 * mm});
            skCircle(sketch, "E12.7.0.47", {"center": v(-27.96, -42.52) * mm, "radius": 2.54 * mm});
            skLineSegment(sketch, "E12.7.0.48", {"start": v(-60.48, -42.52) * mm, "end": v(-52.35, -42.52) * mm, "construction": true});
            skCircle(sketch, "E12.8.0.0", {"center": v(45.24, -50.65) * mm, "radius": 2.54 * mm});
            skCircle(sketch, "E12.8.0.1", {"center": v(-52.3, -50.65) * mm, "radius": 2.54 * mm});
            skLineSegment(sketch, "E12.8.0.2", {"start": v(-60.42, -50.65) * mm, "end": v(-52.3, -50.65) * mm, "construction": true});
            skCircle(sketch, "E12.8.0.3", {"center": v(-36.04, -50.65) * mm, "radius": 3.6 * mm});
            skCircle(sketch, "E12.8.0.4", {"center": v(-3.53, -50.65) * mm, "radius": 3.6 * mm});
            skCircle(sketch, "E12.8.0.5", {"center": v(45.24, -50.65) * mm, "radius": 3.6 * mm});
            skCircle(sketch, "E12.8.0.6", {"center": v(37.11, -50.65) * mm, "radius": 3.6 * mm});
            skCircle(sketch, "E12.8.0.7", {"center": v(53.37, -50.65) * mm, "radius": 3.6 * mm});
            skCircle(sketch, "E12.8.0.8", {"center": v(-11.66, -50.65) * mm, "radius": 3.05 * mm});
            skCircle(sketch, "E12.8.0.9", {"center": v(20.86, -50.65) * mm, "radius": 3.6 * mm});
            skCircle(sketch, "E12.8.0.10", {"center": v(-11.66, -50.65) * mm, "radius": 2.54 * mm});
            skCircle(sketch, "E12.8.0.11", {"center": v(28.98, -50.65) * mm, "radius": 2.54 * mm});
            skCircle(sketch, "E12.8.0.12", {"center": v(4.6, -50.65) * mm, "radius": 2.54 * mm});
            skCircle(sketch, "E12.8.0.13", {"center": v(-27.91, -50.65) * mm, "radius": 3.6 * mm});
            skCircle(sketch, "E12.8.0.14", {"center": v(-27.91, -50.65) * mm, "radius": 3.05 * mm});
            skCircle(sketch, "E12.8.0.15", {"center": v(4.6, -50.65) * mm, "radius": 3.6 * mm});
            skCircle(sketch, "E12.8.0.16", {"center": v(12.73, -50.65) * mm, "radius": 3.6 * mm});
            skCircle(sketch, "E12.8.0.17", {"center": v(-19.78, -50.65) * mm, "radius": 2.54 * mm});
            skCircle(sketch, "E12.8.0.18", {"center": v(-19.78, -50.65) * mm, "radius": 3.05 * mm});
            skCircle(sketch, "E12.8.0.19", {"center": v(28.98, -50.65) * mm, "radius": 3.05 * mm});
            skLineSegment(sketch, "E12.8.0.20", {"start": v(-60.42, -50.65) * mm, "end": v(-60.35, -58.78) * mm, "construction": true});
            skCircle(sketch, "E12.8.0.21", {"center": v(-36.04, -50.65) * mm, "radius": 3.05 * mm});
            skCircle(sketch, "E12.8.0.22", {"center": v(-11.66, -50.65) * mm, "radius": 3.6 * mm});
            skCircle(sketch, "E12.8.0.23", {"center": v(-44.17, -50.65) * mm, "radius": 3.05 * mm});
            skCircle(sketch, "E12.8.0.24", {"center": v(28.98, -50.65) * mm, "radius": 3.6 * mm});
            skCircle(sketch, "E12.8.0.25", {"center": v(-19.78, -50.65) * mm, "radius": 3.6 * mm});
            skCircle(sketch, "E12.8.0.26", {"center": v(-44.17, -50.65) * mm, "radius": 2.54 * mm});
            skCircle(sketch, "E12.8.0.27", {"center": v(-60.42, -50.65) * mm, "radius": 3.6 * mm});
            skCircle(sketch, "E12.8.0.28", {"center": v(-36.04, -50.65) * mm, "radius": 2.54 * mm});
            skCircle(sketch, "E12.8.0.29", {"center": v(20.86, -50.65) * mm, "radius": 3.05 * mm});
            skCircle(sketch, "E12.8.0.30", {"center": v(-52.3, -50.65) * mm, "radius": 3.05 * mm});
            skCircle(sketch, "E12.8.0.31", {"center": v(53.37, -50.65) * mm, "radius": 3.05 * mm});
            skCircle(sketch, "E12.8.0.32", {"center": v(-3.53, -50.65) * mm, "radius": 3.05 * mm});
            skCircle(sketch, "E12.8.0.33", {"center": v(12.73, -50.65) * mm, "radius": 2.54 * mm});
            skCircle(sketch, "E12.8.0.34", {"center": v(37.11, -50.65) * mm, "radius": 2.54 * mm});
            skCircle(sketch, "E12.8.0.35", {"center": v(-44.17, -50.65) * mm, "radius": 3.6 * mm});
            skCircle(sketch, "E12.8.0.36", {"center": v(-52.3, -50.65) * mm, "radius": 3.6 * mm});
            skCircle(sketch, "E12.8.0.37", {"center": v(-3.53, -50.65) * mm, "radius": 2.54 * mm});
            skCircle(sketch, "E12.8.0.38", {"center": v(37.11, -50.65) * mm, "radius": 3.05 * mm});
            skCircle(sketch, "E12.8.0.39", {"center": v(4.6, -50.65) * mm, "radius": 3.05 * mm});
            skCircle(sketch, "E12.8.0.40", {"center": v(12.73, -50.65) * mm, "radius": 3.05 * mm});
            skCircle(sketch, "E12.8.0.41", {"center": v(53.37, -50.65) * mm, "radius": 2.54 * mm});
            skCircle(sketch, "E12.8.0.42", {"center": v(20.86, -50.65) * mm, "radius": 2.54 * mm});
            skCircle(sketch, "E12.8.0.43", {"center": v(-60.42, -50.65) * mm, "radius": 3.05 * mm});
            skCircle(sketch, "E12.8.0.44", {"center": v(45.24, -50.65) * mm, "radius": 3.05 * mm});
            skLineSegment(sketch, "E12.8.0.45", {"start": v(-60.42, -50.65) * mm, "end": v(-52.3, -50.65) * mm, "construction": true});
            skCircle(sketch, "E12.8.0.46", {"center": v(-60.42, -50.65) * mm, "radius": 2.54 * mm});
            skCircle(sketch, "E12.8.0.47", {"center": v(-27.91, -50.65) * mm, "radius": 2.54 * mm});
            skLineSegment(sketch, "E12.8.0.48", {"start": v(-60.42, -50.65) * mm, "end": v(-52.3, -50.65) * mm, "construction": true});
            skCircle(sketch, "E12.9.0.0", {"center": v(45.3, -58.78) * mm, "radius": 2.54 * mm});
            skCircle(sketch, "E12.9.0.1", {"center": v(-52.24, -58.78) * mm, "radius": 2.54 * mm});
            skLineSegment(sketch, "E12.9.0.2", {"start": v(-60.37, -58.78) * mm, "end": v(-52.24, -58.78) * mm, "construction": true});
            skCircle(sketch, "E12.9.0.3", {"center": v(-35.99, -58.78) * mm, "radius": 3.6 * mm});
            skCircle(sketch, "E12.9.0.4", {"center": v(-3.48, -58.78) * mm, "radius": 3.6 * mm});
            skCircle(sketch, "E12.9.0.5", {"center": v(45.3, -58.78) * mm, "radius": 3.6 * mm});
            skCircle(sketch, "E12.9.0.6", {"center": v(37.16, -58.78) * mm, "radius": 3.6 * mm});
            skCircle(sketch, "E12.9.0.7", {"center": v(53.42, -58.78) * mm, "radius": 3.6 * mm});
            skCircle(sketch, "E12.9.0.8", {"center": v(-11.6, -58.78) * mm, "radius": 3.05 * mm});
            skCircle(sketch, "E12.9.0.9", {"center": v(20.9, -58.78) * mm, "radius": 3.6 * mm});
            skCircle(sketch, "E12.9.0.10", {"center": v(-11.6, -58.78) * mm, "radius": 2.54 * mm});
            skCircle(sketch, "E12.9.0.11", {"center": v(29.04, -58.78) * mm, "radius": 2.54 * mm});
            skCircle(sketch, "E12.9.0.12", {"center": v(4.65, -58.78) * mm, "radius": 2.54 * mm});
            skCircle(sketch, "E12.9.0.13", {"center": v(-27.86, -58.78) * mm, "radius": 3.6 * mm});
            skCircle(sketch, "E12.9.0.14", {"center": v(-27.86, -58.78) * mm, "radius": 3.05 * mm});
            skCircle(sketch, "E12.9.0.15", {"center": v(4.65, -58.78) * mm, "radius": 3.6 * mm});
            skCircle(sketch, "E12.9.0.16", {"center": v(12.78, -58.78) * mm, "radius": 3.6 * mm});
            skCircle(sketch, "E12.9.0.17", {"center": v(-19.73, -58.78) * mm, "radius": 2.54 * mm});
            skCircle(sketch, "E12.9.0.18", {"center": v(-19.73, -58.78) * mm, "radius": 3.05 * mm});
            skCircle(sketch, "E12.9.0.19", {"center": v(29.04, -58.78) * mm, "radius": 3.05 * mm});
            skLineSegment(sketch, "E12.9.0.20", {"start": v(-60.37, -58.78) * mm, "end": v(-60.3, -66.9) * mm, "construction": true});
            skCircle(sketch, "E12.9.0.21", {"center": v(-35.99, -58.78) * mm, "radius": 3.05 * mm});
            skCircle(sketch, "E12.9.0.22", {"center": v(-11.6, -58.78) * mm, "radius": 3.6 * mm});
            skCircle(sketch, "E12.9.0.23", {"center": v(-44.12, -58.78) * mm, "radius": 3.05 * mm});
            skCircle(sketch, "E12.9.0.24", {"center": v(29.04, -58.78) * mm, "radius": 3.6 * mm});
            skCircle(sketch, "E12.9.0.25", {"center": v(-19.73, -58.78) * mm, "radius": 3.6 * mm});
            skCircle(sketch, "E12.9.0.26", {"center": v(-44.12, -58.78) * mm, "radius": 2.54 * mm});
            skCircle(sketch, "E12.9.0.27", {"center": v(-60.37, -58.78) * mm, "radius": 3.6 * mm});
            skCircle(sketch, "E12.9.0.28", {"center": v(-35.99, -58.78) * mm, "radius": 2.54 * mm});
            skCircle(sketch, "E12.9.0.29", {"center": v(20.9, -58.78) * mm, "radius": 3.05 * mm});
            skCircle(sketch, "E12.9.0.30", {"center": v(-52.24, -58.78) * mm, "radius": 3.05 * mm});
            skCircle(sketch, "E12.9.0.31", {"center": v(53.42, -58.78) * mm, "radius": 3.05 * mm});
            skCircle(sketch, "E12.9.0.32", {"center": v(-3.48, -58.78) * mm, "radius": 3.05 * mm});
            skCircle(sketch, "E12.9.0.33", {"center": v(12.78, -58.78) * mm, "radius": 2.54 * mm});
            skCircle(sketch, "E12.9.0.34", {"center": v(37.16, -58.78) * mm, "radius": 2.54 * mm});
            skCircle(sketch, "E12.9.0.35", {"center": v(-44.12, -58.78) * mm, "radius": 3.6 * mm});
            skCircle(sketch, "E12.9.0.36", {"center": v(-52.24, -58.78) * mm, "radius": 3.6 * mm});
            skCircle(sketch, "E12.9.0.37", {"center": v(-3.48, -58.78) * mm, "radius": 2.54 * mm});
            skCircle(sketch, "E12.9.0.38", {"center": v(37.16, -58.78) * mm, "radius": 3.05 * mm});
            skCircle(sketch, "E12.9.0.39", {"center": v(4.65, -58.78) * mm, "radius": 3.05 * mm});
            skCircle(sketch, "E12.9.0.40", {"center": v(12.78, -58.78) * mm, "radius": 3.05 * mm});
            skCircle(sketch, "E12.9.0.41", {"center": v(53.42, -58.78) * mm, "radius": 2.54 * mm});
            skCircle(sketch, "E12.9.0.42", {"center": v(20.9, -58.78) * mm, "radius": 2.54 * mm});
            skCircle(sketch, "E12.9.0.43", {"center": v(-60.37, -58.78) * mm, "radius": 3.05 * mm});
            skCircle(sketch, "E12.9.0.44", {"center": v(45.3, -58.78) * mm, "radius": 3.05 * mm});
            skLineSegment(sketch, "E12.9.0.45", {"start": v(-60.37, -58.78) * mm, "end": v(-52.24, -58.78) * mm, "construction": true});
            skCircle(sketch, "E12.9.0.46", {"center": v(-60.37, -58.78) * mm, "radius": 2.54 * mm});
            skCircle(sketch, "E12.9.0.47", {"center": v(-27.86, -58.78) * mm, "radius": 2.54 * mm});
            skLineSegment(sketch, "E12.9.0.48", {"start": v(-60.37, -58.78) * mm, "end": v(-52.24, -58.78) * mm, "construction": true});
            skCircle(sketch, "E12.10.0.0", {"center": v(45.35, -66.9) * mm, "radius": 2.54 * mm});
            skCircle(sketch, "E12.10.0.1", {"center": v(-52.2, -66.9) * mm, "radius": 2.54 * mm});
            skLineSegment(sketch, "E12.10.0.2", {"start": v(-60.32, -66.9) * mm, "end": v(-52.2, -66.9) * mm, "construction": true});
            skCircle(sketch, "E12.10.0.3", {"center": v(-35.93, -66.9) * mm, "radius": 3.6 * mm});
            skCircle(sketch, "E12.10.0.4", {"center": v(-3.42, -66.9) * mm, "radius": 3.6 * mm});
            skCircle(sketch, "E12.10.0.5", {"center": v(45.35, -66.9) * mm, "radius": 3.6 * mm});
            skCircle(sketch, "E12.10.0.6", {"center": v(37.22, -66.9) * mm, "radius": 3.6 * mm});
            skCircle(sketch, "E12.10.0.7", {"center": v(53.47, -66.9) * mm, "radius": 3.6 * mm});
            skCircle(sketch, "E12.10.0.8", {"center": v(-11.55, -66.9) * mm, "radius": 3.05 * mm});
            skCircle(sketch, "E12.10.0.9", {"center": v(20.96, -66.9) * mm, "radius": 3.6 * mm});
            skCircle(sketch, "E12.10.0.10", {"center": v(-11.55, -66.9) * mm, "radius": 2.54 * mm});
            skCircle(sketch, "E12.10.0.11", {"center": v(29.09, -66.9) * mm, "radius": 2.54 * mm});
            skCircle(sketch, "E12.10.0.12", {"center": v(4.7, -66.9) * mm, "radius": 2.54 * mm});
            skCircle(sketch, "E12.10.0.13", {"center": v(-27.8, -66.9) * mm, "radius": 3.6 * mm});
            skCircle(sketch, "E12.10.0.14", {"center": v(-27.8, -66.9) * mm, "radius": 3.05 * mm});
            skCircle(sketch, "E12.10.0.15", {"center": v(4.7, -66.9) * mm, "radius": 3.6 * mm});
            skCircle(sketch, "E12.10.0.16", {"center": v(12.83, -66.9) * mm, "radius": 3.6 * mm});
            skCircle(sketch, "E12.10.0.17", {"center": v(-19.68, -66.9) * mm, "radius": 2.54 * mm});
            skCircle(sketch, "E12.10.0.18", {"center": v(-19.68, -66.9) * mm, "radius": 3.05 * mm});
            skCircle(sketch, "E12.10.0.19", {"center": v(29.09, -66.9) * mm, "radius": 3.05 * mm});
            skLineSegment(sketch, "E12.10.0.20", {"start": v(-60.32, -66.9) * mm, "end": v(-60.25, -75.04) * mm, "construction": true});
            skCircle(sketch, "E12.10.0.21", {"center": v(-35.93, -66.9) * mm, "radius": 3.05 * mm});
            skCircle(sketch, "E12.10.0.22", {"center": v(-11.55, -66.9) * mm, "radius": 3.6 * mm});
            skCircle(sketch, "E12.10.0.23", {"center": v(-44.06, -66.9) * mm, "radius": 3.05 * mm});
            skCircle(sketch, "E12.10.0.24", {"center": v(29.09, -66.9) * mm, "radius": 3.6 * mm});
            skCircle(sketch, "E12.10.0.25", {"center": v(-19.68, -66.9) * mm, "radius": 3.6 * mm});
            skCircle(sketch, "E12.10.0.26", {"center": v(-44.06, -66.9) * mm, "radius": 2.54 * mm});
            skCircle(sketch, "E12.10.0.27", {"center": v(-60.32, -66.9) * mm, "radius": 3.6 * mm});
            skCircle(sketch, "E12.10.0.28", {"center": v(-35.93, -66.9) * mm, "radius": 2.54 * mm});
            skCircle(sketch, "E12.10.0.29", {"center": v(20.96, -66.9) * mm, "radius": 3.05 * mm});
            skCircle(sketch, "E12.10.0.30", {"center": v(-52.2, -66.9) * mm, "radius": 3.05 * mm});
            skCircle(sketch, "E12.10.0.31", {"center": v(53.47, -66.9) * mm, "radius": 3.05 * mm});
            skCircle(sketch, "E12.10.0.32", {"center": v(-3.42, -66.9) * mm, "radius": 3.05 * mm});
            skCircle(sketch, "E12.10.0.33", {"center": v(12.83, -66.9) * mm, "radius": 2.54 * mm});
            skCircle(sketch, "E12.10.0.34", {"center": v(37.22, -66.9) * mm, "radius": 2.54 * mm});
            skCircle(sketch, "E12.10.0.35", {"center": v(-44.06, -66.9) * mm, "radius": 3.6 * mm});
            skCircle(sketch, "E12.10.0.36", {"center": v(-52.2, -66.9) * mm, "radius": 3.6 * mm});
            skCircle(sketch, "E12.10.0.37", {"center": v(-3.42, -66.9) * mm, "radius": 2.54 * mm});
            skCircle(sketch, "E12.10.0.38", {"center": v(37.22, -66.9) * mm, "radius": 3.05 * mm});
            skCircle(sketch, "E12.10.0.39", {"center": v(4.7, -66.9) * mm, "radius": 3.05 * mm});
            skCircle(sketch, "E12.10.0.40", {"center": v(12.83, -66.9) * mm, "radius": 3.05 * mm});
            skCircle(sketch, "E12.10.0.41", {"center": v(53.47, -66.9) * mm, "radius": 2.54 * mm});
            skCircle(sketch, "E12.10.0.42", {"center": v(20.96, -66.9) * mm, "radius": 2.54 * mm});
            skCircle(sketch, "E12.10.0.43", {"center": v(-60.32, -66.9) * mm, "radius": 3.05 * mm});
            skCircle(sketch, "E12.10.0.44", {"center": v(45.35, -66.9) * mm, "radius": 3.05 * mm});
            skLineSegment(sketch, "E12.10.0.45", {"start": v(-60.32, -66.9) * mm, "end": v(-52.2, -66.9) * mm, "construction": true});
            skCircle(sketch, "E12.10.0.46", {"center": v(-60.32, -66.9) * mm, "radius": 2.54 * mm});
            skCircle(sketch, "E12.10.0.47", {"center": v(-27.8, -66.9) * mm, "radius": 2.54 * mm});
            skLineSegment(sketch, "E12.10.0.48", {"start": v(-60.32, -66.9) * mm, "end": v(-52.2, -66.9) * mm, "construction": true});
            skCircle(sketch, "E12.11.0.0", {"center": v(45.4, -75.04) * mm, "radius": 2.54 * mm});
            skCircle(sketch, "E12.11.0.1", {"center": v(-52.14, -75.04) * mm, "radius": 2.54 * mm});
            skLineSegment(sketch, "E12.11.0.2", {"start": v(-60.27, -75.04) * mm, "end": v(-52.14, -75.04) * mm, "construction": true});
            skCircle(sketch, "E12.11.0.3", {"center": v(-35.88, -75.04) * mm, "radius": 3.6 * mm});
            skCircle(sketch, "E12.11.0.4", {"center": v(-3.37, -75.04) * mm, "radius": 3.6 * mm});
            skCircle(sketch, "E12.11.0.5", {"center": v(45.4, -75.04) * mm, "radius": 3.6 * mm});
            skCircle(sketch, "E12.11.0.6", {"center": v(37.27, -75.04) * mm, "radius": 3.6 * mm});
            skCircle(sketch, "E12.11.0.7", {"center": v(53.53, -75.04) * mm, "radius": 3.6 * mm});
            skCircle(sketch, "E12.11.0.8", {"center": v(-11.5, -75.04) * mm, "radius": 3.05 * mm});
            skCircle(sketch, "E12.11.0.9", {"center": v(21.01, -75.04) * mm, "radius": 3.6 * mm});
            skCircle(sketch, "E12.11.0.10", {"center": v(-11.5, -75.04) * mm, "radius": 2.54 * mm});
            skCircle(sketch, "E12.11.0.11", {"center": v(29.14, -75.04) * mm, "radius": 2.54 * mm});
            skCircle(sketch, "E12.11.0.12", {"center": v(4.76, -75.04) * mm, "radius": 2.54 * mm});
            skCircle(sketch, "E12.11.0.13", {"center": v(-27.75, -75.04) * mm, "radius": 3.6 * mm});
            skCircle(sketch, "E12.11.0.14", {"center": v(-27.75, -75.04) * mm, "radius": 3.05 * mm});
            skCircle(sketch, "E12.11.0.15", {"center": v(4.76, -75.04) * mm, "radius": 3.6 * mm});
            skCircle(sketch, "E12.11.0.16", {"center": v(12.89, -75.04) * mm, "radius": 3.6 * mm});
            skCircle(sketch, "E12.11.0.17", {"center": v(-19.63, -75.04) * mm, "radius": 2.54 * mm});
            skCircle(sketch, "E12.11.0.18", {"center": v(-19.63, -75.04) * mm, "radius": 3.05 * mm});
            skCircle(sketch, "E12.11.0.19", {"center": v(29.14, -75.04) * mm, "radius": 3.05 * mm});
            skLineSegment(sketch, "E12.11.0.20", {"start": v(-60.27, -75.04) * mm, "end": v(-60.2, -83.16) * mm, "construction": true});
            skCircle(sketch, "E12.11.0.21", {"center": v(-35.88, -75.04) * mm, "radius": 3.05 * mm});
            skCircle(sketch, "E12.11.0.22", {"center": v(-11.5, -75.04) * mm, "radius": 3.6 * mm});
            skCircle(sketch, "E12.11.0.23", {"center": v(-44.01, -75.04) * mm, "radius": 3.05 * mm});
            skCircle(sketch, "E12.11.0.24", {"center": v(29.14, -75.04) * mm, "radius": 3.6 * mm});
            skCircle(sketch, "E12.11.0.25", {"center": v(-19.63, -75.04) * mm, "radius": 3.6 * mm});
            skCircle(sketch, "E12.11.0.26", {"center": v(-44.01, -75.04) * mm, "radius": 2.54 * mm});
            skCircle(sketch, "E12.11.0.27", {"center": v(-60.27, -75.04) * mm, "radius": 3.6 * mm});
            skCircle(sketch, "E12.11.0.28", {"center": v(-35.88, -75.04) * mm, "radius": 2.54 * mm});
            skCircle(sketch, "E12.11.0.29", {"center": v(21.01, -75.04) * mm, "radius": 3.05 * mm});
            skCircle(sketch, "E12.11.0.30", {"center": v(-52.14, -75.04) * mm, "radius": 3.05 * mm});
            skCircle(sketch, "E12.11.0.31", {"center": v(53.53, -75.04) * mm, "radius": 3.05 * mm});
            skCircle(sketch, "E12.11.0.32", {"center": v(-3.37, -75.04) * mm, "radius": 3.05 * mm});
            skCircle(sketch, "E12.11.0.33", {"center": v(12.89, -75.04) * mm, "radius": 2.54 * mm});
            skCircle(sketch, "E12.11.0.34", {"center": v(37.27, -75.04) * mm, "radius": 2.54 * mm});
            skCircle(sketch, "E12.11.0.35", {"center": v(-44.01, -75.04) * mm, "radius": 3.6 * mm});
            skCircle(sketch, "E12.11.0.36", {"center": v(-52.14, -75.04) * mm, "radius": 3.6 * mm});
            skCircle(sketch, "E12.11.0.37", {"center": v(-3.37, -75.04) * mm, "radius": 2.54 * mm});
            skCircle(sketch, "E12.11.0.38", {"center": v(37.27, -75.04) * mm, "radius": 3.05 * mm});
            skCircle(sketch, "E12.11.0.39", {"center": v(4.76, -75.04) * mm, "radius": 3.05 * mm});
            skCircle(sketch, "E12.11.0.40", {"center": v(12.89, -75.04) * mm, "radius": 3.05 * mm});
            skCircle(sketch, "E12.11.0.41", {"center": v(53.53, -75.04) * mm, "radius": 2.54 * mm});
            skCircle(sketch, "E12.11.0.42", {"center": v(21.01, -75.04) * mm, "radius": 2.54 * mm});
            skCircle(sketch, "E12.11.0.43", {"center": v(-60.27, -75.04) * mm, "radius": 3.05 * mm});
            skCircle(sketch, "E12.11.0.44", {"center": v(45.4, -75.04) * mm, "radius": 3.05 * mm});
            skLineSegment(sketch, "E12.11.0.45", {"start": v(-60.27, -75.04) * mm, "end": v(-52.14, -75.04) * mm, "construction": true});
            skCircle(sketch, "E12.11.0.46", {"center": v(-60.27, -75.04) * mm, "radius": 2.54 * mm});
            skCircle(sketch, "E12.11.0.47", {"center": v(-27.75, -75.04) * mm, "radius": 2.54 * mm});
            skLineSegment(sketch, "E12.11.0.48", {"start": v(-60.27, -75.04) * mm, "end": v(-52.14, -75.04) * mm, "construction": true});
            skCircle(sketch, "E12.12.0.0", {"center": v(45.45, -83.16) * mm, "radius": 2.54 * mm});
            skCircle(sketch, "E12.12.0.1", {"center": v(-52.09, -83.16) * mm, "radius": 2.54 * mm});
            skLineSegment(sketch, "E12.12.0.2", {"start": v(-60.21, -83.16) * mm, "end": v(-52.09, -83.16) * mm, "construction": true});
            skCircle(sketch, "E12.12.0.3", {"center": v(-35.83, -83.16) * mm, "radius": 3.6 * mm});
            skCircle(sketch, "E12.12.0.4", {"center": v(-3.32, -83.16) * mm, "radius": 3.6 * mm});
            skCircle(sketch, "E12.12.0.5", {"center": v(45.45, -83.16) * mm, "radius": 3.6 * mm});
            skCircle(sketch, "E12.12.0.6", {"center": v(37.32, -83.16) * mm, "radius": 3.6 * mm});
            skCircle(sketch, "E12.12.0.7", {"center": v(53.58, -83.16) * mm, "radius": 3.6 * mm});
            skCircle(sketch, "E12.12.0.8", {"center": v(-11.45, -83.16) * mm, "radius": 3.05 * mm});
            skCircle(sketch, "E12.12.0.9", {"center": v(21.07, -83.16) * mm, "radius": 3.6 * mm});
            skCircle(sketch, "E12.12.0.10", {"center": v(-11.45, -83.16) * mm, "radius": 2.54 * mm});
            skCircle(sketch, "E12.12.0.11", {"center": v(29.2, -83.16) * mm, "radius": 2.54 * mm});
            skCircle(sketch, "E12.12.0.12", {"center": v(4.8, -83.16) * mm, "radius": 2.54 * mm});
            skCircle(sketch, "E12.12.0.13", {"center": v(-27.7, -83.16) * mm, "radius": 3.6 * mm});
            skCircle(sketch, "E12.12.0.14", {"center": v(-27.7, -83.16) * mm, "radius": 3.05 * mm});
            skCircle(sketch, "E12.12.0.15", {"center": v(4.8, -83.16) * mm, "radius": 3.6 * mm});
            skCircle(sketch, "E12.12.0.16", {"center": v(12.94, -83.16) * mm, "radius": 3.6 * mm});
            skCircle(sketch, "E12.12.0.17", {"center": v(-19.57, -83.16) * mm, "radius": 2.54 * mm});
            skCircle(sketch, "E12.12.0.18", {"center": v(-19.57, -83.16) * mm, "radius": 3.05 * mm});
            skCircle(sketch, "E12.12.0.19", {"center": v(29.2, -83.16) * mm, "radius": 3.05 * mm});
            skLineSegment(sketch, "E12.12.0.20", {"start": v(-60.21, -83.16) * mm, "end": v(-60.14, -91.3) * mm, "construction": true});
            skCircle(sketch, "E12.12.0.21", {"center": v(-35.83, -83.16) * mm, "radius": 3.05 * mm});
            skCircle(sketch, "E12.12.0.22", {"center": v(-11.45, -83.16) * mm, "radius": 3.6 * mm});
            skCircle(sketch, "E12.12.0.23", {"center": v(-43.96, -83.16) * mm, "radius": 3.05 * mm});
            skCircle(sketch, "E12.12.0.24", {"center": v(29.2, -83.16) * mm, "radius": 3.6 * mm});
            skCircle(sketch, "E12.12.0.25", {"center": v(-19.57, -83.16) * mm, "radius": 3.6 * mm});
            skCircle(sketch, "E12.12.0.26", {"center": v(-43.96, -83.16) * mm, "radius": 2.54 * mm});
            skCircle(sketch, "E12.12.0.27", {"center": v(-60.21, -83.16) * mm, "radius": 3.6 * mm});
            skCircle(sketch, "E12.12.0.28", {"center": v(-35.83, -83.16) * mm, "radius": 2.54 * mm});
            skCircle(sketch, "E12.12.0.29", {"center": v(21.07, -83.16) * mm, "radius": 3.05 * mm});
            skCircle(sketch, "E12.12.0.30", {"center": v(-52.09, -83.16) * mm, "radius": 3.05 * mm});
            skCircle(sketch, "E12.12.0.31", {"center": v(53.58, -83.16) * mm, "radius": 3.05 * mm});
            skCircle(sketch, "E12.12.0.32", {"center": v(-3.32, -83.16) * mm, "radius": 3.05 * mm});
            skCircle(sketch, "E12.12.0.33", {"center": v(12.94, -83.16) * mm, "radius": 2.54 * mm});
            skCircle(sketch, "E12.12.0.34", {"center": v(37.32, -83.16) * mm, "radius": 2.54 * mm});
            skCircle(sketch, "E12.12.0.35", {"center": v(-43.96, -83.16) * mm, "radius": 3.6 * mm});
            skCircle(sketch, "E12.12.0.36", {"center": v(-52.09, -83.16) * mm, "radius": 3.6 * mm});
            skCircle(sketch, "E12.12.0.37", {"center": v(-3.32, -83.16) * mm, "radius": 2.54 * mm});
            skCircle(sketch, "E12.12.0.38", {"center": v(37.32, -83.16) * mm, "radius": 3.05 * mm});
            skCircle(sketch, "E12.12.0.39", {"center": v(4.8, -83.16) * mm, "radius": 3.05 * mm});
            skCircle(sketch, "E12.12.0.40", {"center": v(12.94, -83.16) * mm, "radius": 3.05 * mm});
            skCircle(sketch, "E12.12.0.41", {"center": v(53.58, -83.16) * mm, "radius": 2.54 * mm});
            skCircle(sketch, "E12.12.0.42", {"center": v(21.07, -83.16) * mm, "radius": 2.54 * mm});
            skCircle(sketch, "E12.12.0.43", {"center": v(-60.21, -83.16) * mm, "radius": 3.05 * mm});
            skCircle(sketch, "E12.12.0.44", {"center": v(45.45, -83.16) * mm, "radius": 3.05 * mm});
            skLineSegment(sketch, "E12.12.0.45", {"start": v(-60.21, -83.16) * mm, "end": v(-52.09, -83.16) * mm, "construction": true});
            skCircle(sketch, "E12.12.0.46", {"center": v(-60.21, -83.16) * mm, "radius": 2.54 * mm});
            skCircle(sketch, "E12.12.0.47", {"center": v(-27.7, -83.16) * mm, "radius": 2.54 * mm});
            skLineSegment(sketch, "E12.12.0.48", {"start": v(-60.21, -83.16) * mm, "end": v(-52.09, -83.16) * mm, "construction": true});
            skCircle(sketch, "E12.13.0.0", {"center": v(45.5, -91.3) * mm, "radius": 2.54 * mm});
            skCircle(sketch, "E12.13.0.1", {"center": v(-52.03, -91.3) * mm, "radius": 2.54 * mm});
            skLineSegment(sketch, "E12.13.0.2", {"start": v(-60.16, -91.3) * mm, "end": v(-52.03, -91.3) * mm, "construction": true});
            skCircle(sketch, "E12.13.0.3", {"center": v(-35.78, -91.3) * mm, "radius": 3.6 * mm});
            skCircle(sketch, "E12.13.0.4", {"center": v(-3.27, -91.3) * mm, "radius": 3.6 * mm});
            skCircle(sketch, "E12.13.0.5", {"center": v(45.5, -91.3) * mm, "radius": 3.6 * mm});
            skCircle(sketch, "E12.13.0.6", {"center": v(37.37, -91.3) * mm, "radius": 3.6 * mm});
            skCircle(sketch, "E12.13.0.7", {"center": v(53.63, -91.3) * mm, "radius": 3.6 * mm});
            skCircle(sketch, "E12.13.0.8", {"center": v(-11.4, -91.3) * mm, "radius": 3.05 * mm});
            skCircle(sketch, "E12.13.0.9", {"center": v(21.12, -91.3) * mm, "radius": 3.6 * mm});
            skCircle(sketch, "E12.13.0.10", {"center": v(-11.4, -91.3) * mm, "radius": 2.54 * mm});
            skCircle(sketch, "E12.13.0.11", {"center": v(29.25, -91.3) * mm, "radius": 2.54 * mm});
            skCircle(sketch, "E12.13.0.12", {"center": v(4.86, -91.3) * mm, "radius": 2.54 * mm});
            skCircle(sketch, "E12.13.0.13", {"center": v(-27.65, -91.3) * mm, "radius": 3.6 * mm});
            skCircle(sketch, "E12.13.0.14", {"center": v(-27.65, -91.3) * mm, "radius": 3.05 * mm});
            skCircle(sketch, "E12.13.0.15", {"center": v(4.86, -91.3) * mm, "radius": 3.6 * mm});
            skCircle(sketch, "E12.13.0.16", {"center": v(13, -91.3) * mm, "radius": 3.6 * mm});
            skCircle(sketch, "E12.13.0.17", {"center": v(-19.52, -91.3) * mm, "radius": 2.54 * mm});
            skCircle(sketch, "E12.13.0.18", {"center": v(-19.52, -91.3) * mm, "radius": 3.05 * mm});
            skCircle(sketch, "E12.13.0.19", {"center": v(29.25, -91.3) * mm, "radius": 3.05 * mm});
            skLineSegment(sketch, "E12.13.0.20", {"start": v(-60.16, -91.3) * mm, "end": v(-60.1, -99.42) * mm, "construction": true});
            skCircle(sketch, "E12.13.0.21", {"center": v(-35.78, -91.3) * mm, "radius": 3.05 * mm});
            skCircle(sketch, "E12.13.0.22", {"center": v(-11.4, -91.3) * mm, "radius": 3.6 * mm});
            skCircle(sketch, "E12.13.0.23", {"center": v(-43.9, -91.3) * mm, "radius": 3.05 * mm});
            skCircle(sketch, "E12.13.0.24", {"center": v(29.25, -91.3) * mm, "radius": 3.6 * mm});
            skCircle(sketch, "E12.13.0.25", {"center": v(-19.52, -91.3) * mm, "radius": 3.6 * mm});
            skCircle(sketch, "E12.13.0.26", {"center": v(-43.9, -91.3) * mm, "radius": 2.54 * mm});
            skCircle(sketch, "E12.13.0.27", {"center": v(-60.16, -91.3) * mm, "radius": 3.6 * mm});
            skCircle(sketch, "E12.13.0.28", {"center": v(-35.78, -91.3) * mm, "radius": 2.54 * mm});
            skCircle(sketch, "E12.13.0.29", {"center": v(21.12, -91.3) * mm, "radius": 3.05 * mm});
            skCircle(sketch, "E12.13.0.30", {"center": v(-52.03, -91.3) * mm, "radius": 3.05 * mm});
            skCircle(sketch, "E12.13.0.31", {"center": v(53.63, -91.3) * mm, "radius": 3.05 * mm});
            skCircle(sketch, "E12.13.0.32", {"center": v(-3.27, -91.3) * mm, "radius": 3.05 * mm});
            skCircle(sketch, "E12.13.0.33", {"center": v(13, -91.3) * mm, "radius": 2.54 * mm});
            skCircle(sketch, "E12.13.0.34", {"center": v(37.37, -91.3) * mm, "radius": 2.54 * mm});
            skCircle(sketch, "E12.13.0.35", {"center": v(-43.9, -91.3) * mm, "radius": 3.6 * mm});
            skCircle(sketch, "E12.13.0.36", {"center": v(-52.03, -91.3) * mm, "radius": 3.6 * mm});
            skCircle(sketch, "E12.13.0.37", {"center": v(-3.27, -91.3) * mm, "radius": 2.54 * mm});
            skCircle(sketch, "E12.13.0.38", {"center": v(37.37, -91.3) * mm, "radius": 3.05 * mm});
            skCircle(sketch, "E12.13.0.39", {"center": v(4.86, -91.3) * mm, "radius": 3.05 * mm});
            skCircle(sketch, "E12.13.0.40", {"center": v(13, -91.3) * mm, "radius": 3.05 * mm});
            skCircle(sketch, "E12.13.0.41", {"center": v(53.63, -91.3) * mm, "radius": 2.54 * mm});
            skCircle(sketch, "E12.13.0.42", {"center": v(21.12, -91.3) * mm, "radius": 2.54 * mm});
            skCircle(sketch, "E12.13.0.43", {"center": v(-60.16, -91.3) * mm, "radius": 3.05 * mm});
            skCircle(sketch, "E12.13.0.44", {"center": v(45.5, -91.3) * mm, "radius": 3.05 * mm});
            skLineSegment(sketch, "E12.13.0.45", {"start": v(-60.16, -91.3) * mm, "end": v(-52.03, -91.3) * mm, "construction": true});
            skCircle(sketch, "E12.13.0.46", {"center": v(-60.16, -91.3) * mm, "radius": 2.54 * mm});
            skCircle(sketch, "E12.13.0.47", {"center": v(-27.65, -91.3) * mm, "radius": 2.54 * mm});
            skLineSegment(sketch, "E12.13.0.48", {"start": v(-60.16, -91.3) * mm, "end": v(-52.03, -91.3) * mm, "construction": true});
            skCircle(sketch, "E12.14.0.0", {"center": v(45.55, -99.42) * mm, "radius": 2.54 * mm});
            skCircle(sketch, "E12.14.0.1", {"center": v(-51.98, -99.42) * mm, "radius": 2.54 * mm});
            skLineSegment(sketch, "E12.14.0.2", {"start": v(-60.1, -99.42) * mm, "end": v(-51.98, -99.42) * mm, "construction": true});
            skCircle(sketch, "E12.14.0.3", {"center": v(-35.73, -99.42) * mm, "radius": 3.6 * mm});
            skCircle(sketch, "E12.14.0.4", {"center": v(-3.21, -99.42) * mm, "radius": 3.6 * mm});
            skCircle(sketch, "E12.14.0.5", {"center": v(45.55, -99.42) * mm, "radius": 3.6 * mm});
            skCircle(sketch, "E12.14.0.6", {"center": v(37.43, -99.42) * mm, "radius": 3.6 * mm});
            skCircle(sketch, "E12.14.0.7", {"center": v(53.68, -99.42) * mm, "radius": 3.6 * mm});
            skCircle(sketch, "E12.14.0.8", {"center": v(-11.34, -99.42) * mm, "radius": 3.05 * mm});
            skCircle(sketch, "E12.14.0.9", {"center": v(21.17, -99.42) * mm, "radius": 3.6 * mm});
            skCircle(sketch, "E12.14.0.10", {"center": v(-11.34, -99.42) * mm, "radius": 2.54 * mm});
            skCircle(sketch, "E12.14.0.11", {"center": v(29.3, -99.42) * mm, "radius": 2.54 * mm});
            skCircle(sketch, "E12.14.0.12", {"center": v(4.91, -99.42) * mm, "radius": 2.54 * mm});
            skCircle(sketch, "E12.14.0.13", {"center": v(-27.6, -99.42) * mm, "radius": 3.6 * mm});
            skCircle(sketch, "E12.14.0.14", {"center": v(-27.6, -99.42) * mm, "radius": 3.05 * mm});
            skCircle(sketch, "E12.14.0.15", {"center": v(4.91, -99.42) * mm, "radius": 3.6 * mm});
            skCircle(sketch, "E12.14.0.16", {"center": v(13.04, -99.42) * mm, "radius": 3.6 * mm});
            skCircle(sketch, "E12.14.0.17", {"center": v(-19.47, -99.42) * mm, "radius": 2.54 * mm});
            skCircle(sketch, "E12.14.0.18", {"center": v(-19.47, -99.42) * mm, "radius": 3.05 * mm});
            skCircle(sketch, "E12.14.0.19", {"center": v(29.3, -99.42) * mm, "radius": 3.05 * mm});
            skCircle(sketch, "E12.14.0.21", {"center": v(-35.73, -99.42) * mm, "radius": 3.05 * mm});
            skCircle(sketch, "E12.14.0.22", {"center": v(-11.34, -99.42) * mm, "radius": 3.6 * mm});
            skCircle(sketch, "E12.14.0.23", {"center": v(-43.85, -99.42) * mm, "radius": 3.05 * mm});
            skCircle(sketch, "E12.14.0.24", {"center": v(29.3, -99.42) * mm, "radius": 3.6 * mm});
            skCircle(sketch, "E12.14.0.25", {"center": v(-19.47, -99.42) * mm, "radius": 3.6 * mm});
            skCircle(sketch, "E12.14.0.26", {"center": v(-43.85, -99.42) * mm, "radius": 2.54 * mm});
            skCircle(sketch, "E12.14.0.27", {"center": v(-60.1, -99.42) * mm, "radius": 3.6 * mm});
            skCircle(sketch, "E12.14.0.28", {"center": v(-35.73, -99.42) * mm, "radius": 2.54 * mm});
            skCircle(sketch, "E12.14.0.29", {"center": v(21.17, -99.42) * mm, "radius": 3.05 * mm});
            skCircle(sketch, "E12.14.0.30", {"center": v(-51.98, -99.42) * mm, "radius": 3.05 * mm});
            skCircle(sketch, "E12.14.0.31", {"center": v(53.68, -99.42) * mm, "radius": 3.05 * mm});
            skCircle(sketch, "E12.14.0.32", {"center": v(-3.21, -99.42) * mm, "radius": 3.05 * mm});
            skCircle(sketch, "E12.14.0.33", {"center": v(13.04, -99.42) * mm, "radius": 2.54 * mm});
            skCircle(sketch, "E12.14.0.34", {"center": v(37.43, -99.42) * mm, "radius": 2.54 * mm});
            skCircle(sketch, "E12.14.0.35", {"center": v(-43.85, -99.42) * mm, "radius": 3.6 * mm});
            skCircle(sketch, "E12.14.0.36", {"center": v(-51.98, -99.42) * mm, "radius": 3.6 * mm});
            skCircle(sketch, "E12.14.0.37", {"center": v(-3.21, -99.42) * mm, "radius": 2.54 * mm});
            skCircle(sketch, "E12.14.0.38", {"center": v(37.43, -99.42) * mm, "radius": 3.05 * mm});
            skCircle(sketch, "E12.14.0.39", {"center": v(4.91, -99.42) * mm, "radius": 3.05 * mm});
            skCircle(sketch, "E12.14.0.40", {"center": v(13.04, -99.42) * mm, "radius": 3.05 * mm});
            skCircle(sketch, "E12.14.0.41", {"center": v(53.68, -99.42) * mm, "radius": 2.54 * mm});
            skCircle(sketch, "E12.14.0.42", {"center": v(21.17, -99.42) * mm, "radius": 2.54 * mm});
            skCircle(sketch, "E12.14.0.43", {"center": v(-60.1, -99.42) * mm, "radius": 3.05 * mm});
            skCircle(sketch, "E12.14.0.44", {"center": v(45.55, -99.42) * mm, "radius": 3.05 * mm});
            skLineSegment(sketch, "E12.14.0.45", {"start": v(-60.1, -99.42) * mm, "end": v(-51.98, -99.42) * mm, "construction": true});
            skCircle(sketch, "E12.14.0.46", {"center": v(-60.1, -99.42) * mm, "radius": 2.54 * mm});
            skCircle(sketch, "E12.14.0.47", {"center": v(-27.6, -99.42) * mm, "radius": 2.54 * mm});
            skLineSegment(sketch, "E12.direction1", {"start": v(-60.77, 6.24) * mm, "end": v(-60.72, -1.88) * mm, "construction": true});
            skLineSegment(sketch, "E13", {"start": v(-60.96, 17.96) * mm, "end": v(52.83, 17.96) * mm});
            skLineSegment(sketch, "E14", {"start": v(56.54, 14.37) * mm, "end": v(57.27, -99.4) * mm});
            skLineSegment(sketch, "E15", {"start": v(-64.43, 14.37) * mm, "end": v(-63.7, -99.42) * mm});
            skLineSegment(sketch, "E16", {"start": v(-60.1, -103) * mm, "end": v(53.68, -103) * mm});
            skSolve(sketch);
        }
        {
            var Q0;
            Q0=makeQuery(id+"F0.imprint","IMPRINT",FACE,{"disambiguationData":[TD([[makeQuery(id+"F0.imprint","IMPRINT",EDGE,{"derivedFrom":sQuery(id+"F0.wireOp",EDGE,"E12.1.0.3")}),-1.0]])]});
            var Q1;
            Q1 = qSketchRegion(id + "F0", true);
            extrude(context, id + "F1", {"entities" : qUnion([Q0, Q1]), "depth" : 2.03 * mm, "offsetDistance" : 25.4 * mm});
        }
        {
            var Q0;
            Q0=makeQuery(id+"F1.opExtrude","CAP_EDGE",EDGE,{"disambiguationData":[OSD([sQuery(id+"F0.wireOp",EDGE,"E12.1.0.25")])],"isStart":false});
            var Q1;
            Q1=makeQuery(id+"F1.opExtrude","CAP_EDGE",EDGE,{"disambiguationData":[OSD([sQuery(id+"F0.wireOp",EDGE,"E11.0.5.0")])],"isStart":false});
            fillet(context, id + "F2", {"entities" : qUnion([Q0, Q1]), "radius" : 1.27 * mm, "tangentPropagation" : true, "allowEdgeOverflow" : false});
        }
    });
